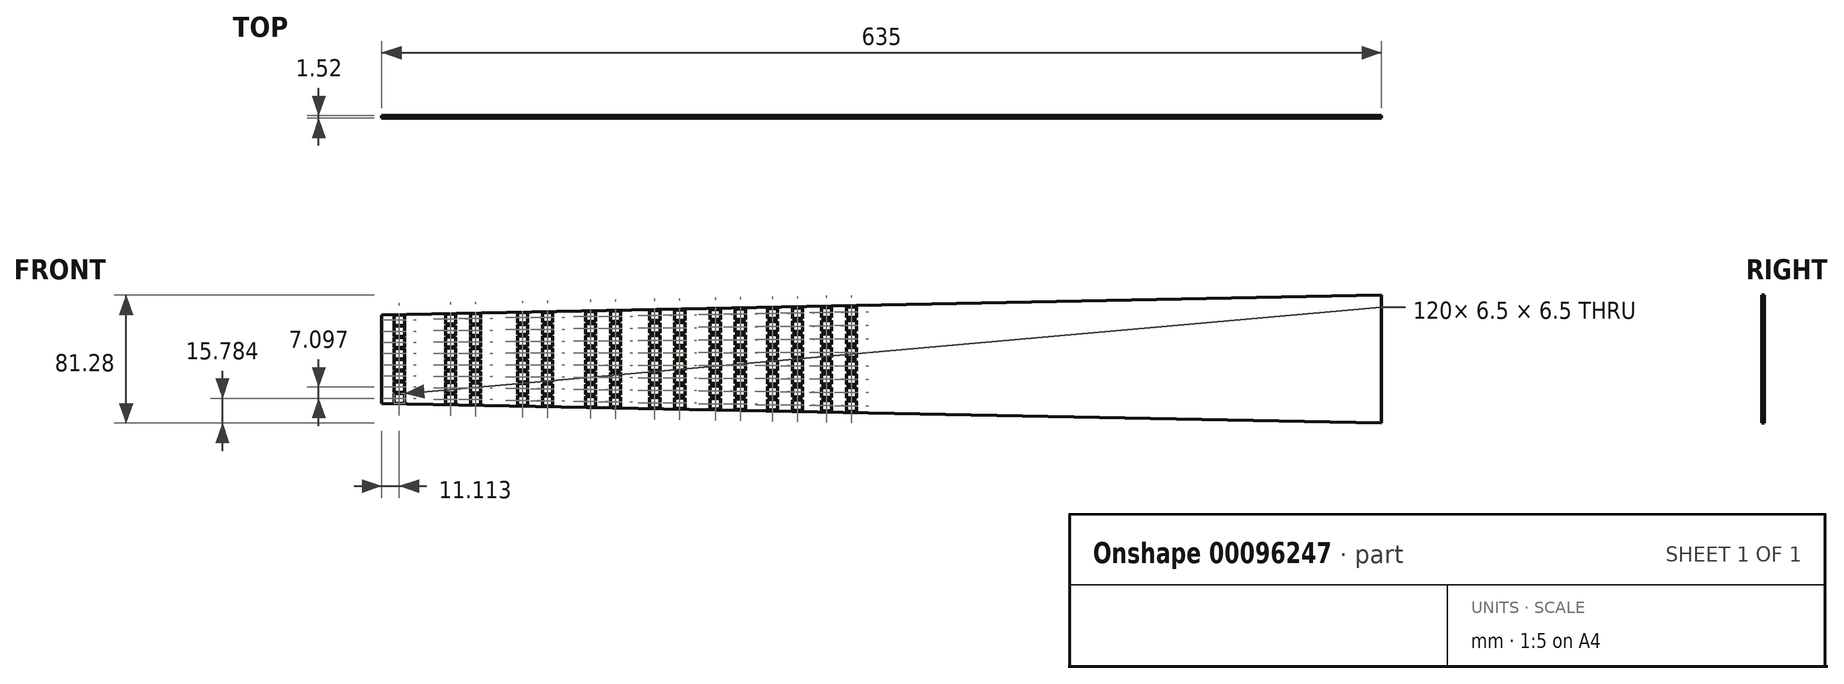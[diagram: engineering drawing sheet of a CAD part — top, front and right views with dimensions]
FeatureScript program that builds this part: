
annotation { "Feature Type Name" : "Feature", "Feature Type Description" : "" }
export const myFeature = defineFeature(function(context is Context, id is Id, definition is map)
    precondition{}
    {
        {
            var Q0;
            Q0=qCreatedBy(makeId("Front.planeOp"),FACE);
            var sketch = newSketch(context, id + "F0", { "sketchPlane" : qUnion([Q0])});
            skLineSegment(sketch, "E0", {"start": v(0, 0) * mm, "end": v(0, 56.39) * mm});
            skLineSegment(sketch, "E1", {"start": v(0, 56.39) * mm, "end": v(304.8, 62.36) * mm});
            skLineSegment(sketch, "E2", {"start": v(635, 68.83) * mm, "end": v(635, -12.45) * mm});
            skLineSegment(sketch, "E3", {"start": v(635, -12.45) * mm, "end": v(304.8, -5.97) * mm});
            skLineSegment(sketch, "E4", {"start": v(0, 28.2) * mm, "end": v(897.35, 28.2) * mm, "construction": true});
            skLineSegment(sketch, "E5", {"start": v(0, 3.52) * mm, "end": v(635, -7.37) * mm, "construction": true});
            skLineSegment(sketch, "E6", {"start": v(0, 10.57) * mm, "end": v(635, 2.8) * mm, "construction": true});
            skLineSegment(sketch, "E7", {"start": v(0, 17.62) * mm, "end": v(635, 12.95) * mm, "construction": true});
            skLineSegment(sketch, "E8", {"start": v(0, 24.67) * mm, "end": v(635, 23.11) * mm, "construction": true});
            skLineSegment(sketch, "E9", {"start": v(11.11, -8.07) * mm, "end": v(11.11, 65.52) * mm, "construction": true});
            skLineSegment(sketch, "E10", {"start": v(59.58, -8.48) * mm, "end": v(59.58, 66.34) * mm, "construction": true});
            skLineSegment(sketch, "E11", {"start": v(43.7, -5.78) * mm, "end": v(43.7, 64.91) * mm, "construction": true});
            skPoint(sketch, "E12", {"position": v(11.11, 3.33) * mm});
            skLineSegment(sketch, "E13.bottom", {"start": v(7.86, 6.58) * mm, "end": v(14.36, 6.58) * mm});
            skLineSegment(sketch, "E13.top", {"start": v(7.86, 0.08) * mm, "end": v(14.36, 0.08) * mm});
            skLineSegment(sketch, "E13.left", {"start": v(7.86, 6.58) * mm, "end": v(7.86, 0.08) * mm});
            skLineSegment(sketch, "E13.right", {"start": v(14.36, 6.58) * mm, "end": v(14.36, 0.08) * mm});
            skLineSegment(sketch, "E14.direction2", {"start": v(7.86, 6.58) * mm, "end": v(7.86, 13.7) * mm, "construction": true});
            skLineSegment(sketch, "E15.bottom", {"start": v(40.46, 6.02) * mm, "end": v(46.96, 6.02) * mm});
            skLineSegment(sketch, "E15.top", {"start": v(40.46, -0.48) * mm, "end": v(46.96, -0.48) * mm});
            skLineSegment(sketch, "E15.left", {"start": v(40.46, 6.02) * mm, "end": v(40.46, -0.48) * mm});
            skLineSegment(sketch, "E15.right", {"start": v(46.96, 6.02) * mm, "end": v(46.96, -0.48) * mm});
            skPoint(sketch, "E15.middle", {"position": v(43.7, 2.77) * mm});
            skLineSegment(sketch, "E16.bottom", {"start": v(62.83, 5.75) * mm, "end": v(56.33, 5.75) * mm});
            skLineSegment(sketch, "E16.top", {"start": v(62.83, -0.75) * mm, "end": v(56.33, -0.75) * mm});
            skLineSegment(sketch, "E16.left", {"start": v(62.83, 5.75) * mm, "end": v(62.83, -0.75) * mm});
            skLineSegment(sketch, "E16.right", {"start": v(56.33, 5.75) * mm, "end": v(56.33, -0.75) * mm});
            skPoint(sketch, "E16.middle", {"position": v(59.58, 2.5) * mm});
            skPoint(sketch, "E17", {"position": v(43.7, 10.04) * mm});
            skPoint(sketch, "E18", {"position": v(59.58, 9.84) * mm});
            skLineSegment(sketch, "E19", {"start": v(89.46, -9.6) * mm, "end": v(89.46, 71.58) * mm, "construction": true});
            skLineSegment(sketch, "E20", {"start": v(105.33, -10.34) * mm, "end": v(105.33, 69.93) * mm, "construction": true});
            skLineSegment(sketch, "E21", {"start": v(132.64, -17.59) * mm, "end": v(132.64, 74.26) * mm, "construction": true});
            skLineSegment(sketch, "E22", {"start": v(148.51, -17.59) * mm, "end": v(148.51, 69.02) * mm, "construction": true});
            skLineSegment(sketch, "E23", {"start": v(173.4, -18.82) * mm, "end": v(173.4, 73.33) * mm, "construction": true});
            skLineSegment(sketch, "E24", {"start": v(189.27, -16.66) * mm, "end": v(189.27, 66.86) * mm, "construction": true});
            skLineSegment(sketch, "E25", {"start": v(451.27, -15.83) * mm, "end": v(451.27, 70.28) * mm, "construction": true});
            skLineSegment(sketch, "E26", {"start": v(227.74, -18.15) * mm, "end": v(227.74, 69.99) * mm, "construction": true});
            skLineSegment(sketch, "E27", {"start": v(264.05, -13.9) * mm, "end": v(264.05, 74.15) * mm, "construction": true});
            skLineSegment(sketch, "E28", {"start": v(298.33, -16.5) * mm, "end": v(298.33, 71.54) * mm, "construction": true});
            skLineSegment(sketch, "E29", {"start": v(330.68, -19.56) * mm, "end": v(330.68, 75.46) * mm, "construction": true});
            skLineSegment(sketch, "E30", {"start": v(361.21, -17.9) * mm, "end": v(361.21, 72.97) * mm, "construction": true});
            skLineSegment(sketch, "E31", {"start": v(390.03, -19.02) * mm, "end": v(390.03, 73.96) * mm, "construction": true});
            skLineSegment(sketch, "E32", {"start": v(417.24, -23.13) * mm, "end": v(417.24, 74.37) * mm, "construction": true});
            skLineSegment(sketch, "E33", {"start": v(442.91, -24.9) * mm, "end": v(442.91, 73.26) * mm, "construction": true});
            skLineSegment(sketch, "E34", {"start": v(467.15, -27.86) * mm, "end": v(467.15, 72.83) * mm, "construction": true});
            skLineSegment(sketch, "E35", {"start": v(492.88, -29.16) * mm, "end": v(492.88, 78.06) * mm, "construction": true});
            skLineSegment(sketch, "E36", {"start": v(513.87, -22.04) * mm, "end": v(513.87, 76.59) * mm, "construction": true});
            skLineSegment(sketch, "E37", {"start": v(533.67, -25.93) * mm, "end": v(533.67, 79.32) * mm, "construction": true});
            skLineSegment(sketch, "E38", {"start": v(602.4, -21.27) * mm, "end": v(602.4, 83.2) * mm, "construction": true});
            skLineSegment(sketch, "E39", {"start": v(570.01, -19.88) * mm, "end": v(570.01, 78.37) * mm, "construction": true});
            skLineSegment(sketch, "E40", {"start": v(586.67, -17.8) * mm, "end": v(586.67, 83.9) * mm, "construction": true});
            skLineSegment(sketch, "E41", {"start": v(552.37, -18.5) * mm, "end": v(552.37, 94.16) * mm, "construction": true});
            skPoint(sketch, "E42", {"position": v(89.46, 2) * mm});
            skPoint(sketch, "E43", {"position": v(89.46, 9.48) * mm});
            skPoint(sketch, "E44", {"position": v(105.33, 9.28) * mm});
            skPoint(sketch, "E45", {"position": v(105.33, 1.72) * mm});
            skPoint(sketch, "E46", {"position": v(132.64, 8.95) * mm});
            skPoint(sketch, "E47", {"position": v(132.64, 1.25) * mm});
            skPoint(sketch, "E48", {"position": v(148.51, 8.75) * mm});
            skPoint(sketch, "E49", {"position": v(148.51, 0.98) * mm});
            skPoint(sketch, "E50", {"position": v(173.4, 8.45) * mm});
            skPoint(sketch, "E51", {"position": v(173.4, 0.55) * mm});
            skPoint(sketch, "E52", {"position": v(189.27, 8.25) * mm});
            skPoint(sketch, "E53", {"position": v(227.74, 7.78) * mm});
            skPoint(sketch, "E54", {"position": v(227.74, -0.38) * mm});
            skLineSegment(sketch, "E55", {"start": v(304.8, -5.97) * mm, "end": v(304.8, 62.36) * mm});
            skLineSegment(sketch, "E56", {"start": v(211.87, -18.15) * mm, "end": v(211.87, 88.54) * mm, "construction": true});
            skLineSegment(sketch, "E57", {"start": v(248.18, -17.72) * mm, "end": v(248.18, 84.91) * mm, "construction": true});
            skLineSegment(sketch, "E58", {"start": v(282.45, -20.3) * mm, "end": v(282.45, 79.21) * mm, "construction": true});
            skPoint(sketch, "E59", {"position": v(298.33, -1.6) * mm});
            skPoint(sketch, "E60", {"position": v(298.33, 6.92) * mm});
            skPoint(sketch, "E61", {"position": v(282.45, 7.11) * mm});
            skPoint(sketch, "E62", {"position": v(282.45, -1.32) * mm});
            skPoint(sketch, "E63", {"position": v(264.05, -1) * mm});
            skPoint(sketch, "E64", {"position": v(264.05, 7.34) * mm});
            skPoint(sketch, "E65", {"position": v(248.18, 7.53) * mm});
            skPoint(sketch, "E66", {"position": v(248.18, -0.73) * mm});
            skPoint(sketch, "E67", {"position": v(211.87, 7.98) * mm});
            skPoint(sketch, "E68", {"position": v(211.87, -0.1) * mm});
            skLineSegment(sketch, "E69.bottom", {"start": v(86.2, 5.24) * mm, "end": v(92.7, 5.24) * mm});
            skLineSegment(sketch, "E69.top", {"start": v(86.2, -1.26) * mm, "end": v(92.7, -1.26) * mm});
            skLineSegment(sketch, "E69.left", {"start": v(86.2, 5.24) * mm, "end": v(86.2, -1.26) * mm});
            skLineSegment(sketch, "E69.right", {"start": v(92.7, 5.24) * mm, "end": v(92.7, -1.26) * mm});
            skLineSegment(sketch, "E70.bottom", {"start": v(102.08, 4.97) * mm, "end": v(108.58, 4.97) * mm});
            skLineSegment(sketch, "E70.top", {"start": v(102.08, -1.53) * mm, "end": v(108.58, -1.53) * mm});
            skLineSegment(sketch, "E70.left", {"start": v(102.08, 4.97) * mm, "end": v(102.08, -1.53) * mm});
            skLineSegment(sketch, "E70.right", {"start": v(108.58, 4.97) * mm, "end": v(108.58, -1.53) * mm});
            skLineSegment(sketch, "E71.bottom", {"start": v(129.39, 4.5) * mm, "end": v(135.89, 4.5) * mm});
            skLineSegment(sketch, "E71.top", {"start": v(129.39, -2) * mm, "end": v(135.89, -2) * mm});
            skLineSegment(sketch, "E71.left", {"start": v(129.39, 4.5) * mm, "end": v(129.39, -2) * mm});
            skLineSegment(sketch, "E71.right", {"start": v(135.89, 4.5) * mm, "end": v(135.89, -2) * mm});
            skLineSegment(sketch, "E72.bottom", {"start": v(145.26, 4.23) * mm, "end": v(151.76, 4.23) * mm});
            skLineSegment(sketch, "E72.top", {"start": v(145.26, -2.27) * mm, "end": v(151.76, -2.27) * mm});
            skLineSegment(sketch, "E72.left", {"start": v(145.26, 4.23) * mm, "end": v(145.26, -2.27) * mm});
            skLineSegment(sketch, "E72.right", {"start": v(151.76, 4.23) * mm, "end": v(151.76, -2.27) * mm});
            skLineSegment(sketch, "E73.bottom", {"start": v(208.62, 3.14) * mm, "end": v(215.12, 3.14) * mm});
            skLineSegment(sketch, "E73.top", {"start": v(208.62, -3.36) * mm, "end": v(215.12, -3.36) * mm});
            skLineSegment(sketch, "E73.left", {"start": v(208.62, 3.14) * mm, "end": v(208.62, -3.36) * mm});
            skLineSegment(sketch, "E73.right", {"start": v(215.12, 3.14) * mm, "end": v(215.12, -3.36) * mm});
            skLineSegment(sketch, "E74.bottom", {"start": v(224.5, 2.87) * mm, "end": v(231, 2.87) * mm});
            skLineSegment(sketch, "E74.top", {"start": v(224.5, -3.63) * mm, "end": v(231, -3.63) * mm});
            skLineSegment(sketch, "E74.left", {"start": v(224.5, 2.87) * mm, "end": v(224.5, -3.63) * mm});
            skLineSegment(sketch, "E74.right", {"start": v(231, 2.87) * mm, "end": v(231, -3.63) * mm});
            skLineSegment(sketch, "E75.bottom", {"start": v(244.93, 2.52) * mm, "end": v(251.43, 2.52) * mm});
            skLineSegment(sketch, "E75.top", {"start": v(244.93, -3.98) * mm, "end": v(251.43, -3.98) * mm});
            skLineSegment(sketch, "E75.left", {"start": v(244.93, 2.52) * mm, "end": v(244.93, -3.98) * mm});
            skLineSegment(sketch, "E75.right", {"start": v(251.43, 2.52) * mm, "end": v(251.43, -3.98) * mm});
            skLineSegment(sketch, "E76.bottom", {"start": v(260.8, 2.25) * mm, "end": v(267.3, 2.25) * mm});
            skLineSegment(sketch, "E76.top", {"start": v(260.8, -4.25) * mm, "end": v(267.3, -4.25) * mm});
            skLineSegment(sketch, "E76.left", {"start": v(260.8, 2.25) * mm, "end": v(260.8, -4.25) * mm});
            skLineSegment(sketch, "E76.right", {"start": v(267.3, 2.25) * mm, "end": v(267.3, -4.25) * mm});
            skLineSegment(sketch, "E77.bottom", {"start": v(279.2, 1.93) * mm, "end": v(285.7, 1.93) * mm});
            skLineSegment(sketch, "E77.top", {"start": v(279.2, -4.57) * mm, "end": v(285.7, -4.57) * mm});
            skLineSegment(sketch, "E77.left", {"start": v(279.2, 1.93) * mm, "end": v(279.2, -4.57) * mm});
            skLineSegment(sketch, "E77.right", {"start": v(285.7, 1.93) * mm, "end": v(285.7, -4.57) * mm});
            skLineSegment(sketch, "E78.bottom", {"start": v(295.08, 1.66) * mm, "end": v(301.58, 1.66) * mm});
            skLineSegment(sketch, "E78.top", {"start": v(295.08, -4.84) * mm, "end": v(301.58, -4.84) * mm});
            skLineSegment(sketch, "E78.left", {"start": v(295.08, 1.66) * mm, "end": v(295.08, -4.84) * mm});
            skLineSegment(sketch, "E78.right", {"start": v(301.58, 1.66) * mm, "end": v(301.58, -4.84) * mm});
            skLineSegment(sketch, "E79.bottom", {"start": v(170.14, 3.8) * mm, "end": v(176.64, 3.8) * mm});
            skLineSegment(sketch, "E79.top", {"start": v(170.14, -2.7) * mm, "end": v(176.64, -2.7) * mm});
            skLineSegment(sketch, "E79.left", {"start": v(170.14, 3.8) * mm, "end": v(170.14, -2.7) * mm});
            skLineSegment(sketch, "E79.right", {"start": v(176.64, 3.8) * mm, "end": v(176.64, -2.7) * mm});
            skPoint(sketch, "E80", {"position": v(304.8, 62.36) * mm});
            skPoint(sketch, "E81", {"position": v(304.8, -5.97) * mm});
            skPoint(sketch, "E82.orphan", {"position": v(304.8, 80.2) * mm});
            skLineSegment(sketch, "E83", {"start": v(304.8, 62.36) * mm, "end": v(635, 68.83) * mm});
            skLineSegment(sketch, "E84", {"start": v(304.8, -5.97) * mm, "end": v(0, 0) * mm});
            skLineSegment(sketch, "E85.0.1.0", {"start": v(40.46, 13.31) * mm, "end": v(46.96, 13.31) * mm});
            skLineSegment(sketch, "E85.0.1.1", {"start": v(40.46, 13.31) * mm, "end": v(40.46, 6.81) * mm});
            skLineSegment(sketch, "E85.0.1.2", {"start": v(46.96, 13.31) * mm, "end": v(46.96, 6.81) * mm});
            skLineSegment(sketch, "E85.0.1.3", {"start": v(40.46, 6.81) * mm, "end": v(46.96, 6.81) * mm});
            skLineSegment(sketch, "E85.0.2.0", {"start": v(40.46, 20.6) * mm, "end": v(46.96, 20.6) * mm});
            skLineSegment(sketch, "E85.0.2.1", {"start": v(40.46, 20.6) * mm, "end": v(40.46, 14.1) * mm});
            skLineSegment(sketch, "E85.0.2.2", {"start": v(46.96, 20.6) * mm, "end": v(46.96, 14.1) * mm});
            skLineSegment(sketch, "E85.0.2.3", {"start": v(40.46, 14.1) * mm, "end": v(46.96, 14.1) * mm});
            skLineSegment(sketch, "E85.0.3.0", {"start": v(40.46, 27.89) * mm, "end": v(46.96, 27.89) * mm});
            skLineSegment(sketch, "E85.0.3.1", {"start": v(40.46, 27.89) * mm, "end": v(40.46, 21.39) * mm});
            skLineSegment(sketch, "E85.0.3.2", {"start": v(46.96, 27.89) * mm, "end": v(46.96, 21.39) * mm});
            skLineSegment(sketch, "E85.0.3.3", {"start": v(40.46, 21.39) * mm, "end": v(46.96, 21.39) * mm});
            skLineSegment(sketch, "E85.direction1", {"start": v(40.46, 6.02) * mm, "end": v(65.86, 6.02) * mm, "construction": true});
            skLineSegment(sketch, "E85.direction2", {"start": v(40.46, 6.02) * mm, "end": v(40.46, 13.31) * mm, "construction": true});
            skLineSegment(sketch, "E86.0.1.0", {"start": v(56.33, 13.1) * mm, "end": v(56.33, 6.6) * mm});
            skLineSegment(sketch, "E86.0.1.1", {"start": v(62.83, 6.6) * mm, "end": v(56.33, 6.6) * mm});
            skLineSegment(sketch, "E86.0.1.2", {"start": v(62.83, 13.1) * mm, "end": v(56.33, 13.1) * mm});
            skLineSegment(sketch, "E86.0.1.3", {"start": v(62.83, 13.1) * mm, "end": v(62.83, 6.6) * mm});
            skPoint(sketch, "E86.0.1.4", {"position": v(59.58, 9.85) * mm});
            skLineSegment(sketch, "E86.0.2.0", {"start": v(56.33, 20.45) * mm, "end": v(56.33, 13.95) * mm});
            skLineSegment(sketch, "E86.0.2.1", {"start": v(62.83, 13.95) * mm, "end": v(56.33, 13.95) * mm});
            skLineSegment(sketch, "E86.0.2.2", {"start": v(62.83, 20.45) * mm, "end": v(56.33, 20.45) * mm});
            skLineSegment(sketch, "E86.0.2.3", {"start": v(62.83, 20.45) * mm, "end": v(62.83, 13.95) * mm});
            skPoint(sketch, "E86.0.2.4", {"position": v(59.58, 17.2) * mm});
            skLineSegment(sketch, "E86.0.3.0", {"start": v(56.33, 27.8) * mm, "end": v(56.33, 21.3) * mm});
            skLineSegment(sketch, "E86.0.3.1", {"start": v(62.83, 21.3) * mm, "end": v(56.33, 21.3) * mm});
            skLineSegment(sketch, "E86.0.3.2", {"start": v(62.83, 27.8) * mm, "end": v(56.33, 27.8) * mm});
            skLineSegment(sketch, "E86.0.3.3", {"start": v(62.83, 27.8) * mm, "end": v(62.83, 21.3) * mm});
            skPoint(sketch, "E86.0.3.4", {"position": v(59.58, 24.55) * mm});
            skLineSegment(sketch, "E86.direction1", {"start": v(56.33, -0.75) * mm, "end": v(83.32, -0.75) * mm, "construction": true});
            skLineSegment(sketch, "E86.direction2", {"start": v(56.33, -0.75) * mm, "end": v(56.33, 6.6) * mm, "construction": true});
            skLineSegment(sketch, "E87.0.1.0", {"start": v(86.2, 6.25) * mm, "end": v(92.7, 6.25) * mm});
            skLineSegment(sketch, "E87.0.1.1", {"start": v(92.7, 12.75) * mm, "end": v(92.7, 6.25) * mm});
            skPoint(sketch, "E87.0.1.2", {"position": v(89.46, 9.5) * mm});
            skLineSegment(sketch, "E87.0.1.3", {"start": v(86.2, 12.75) * mm, "end": v(86.2, 6.25) * mm});
            skLineSegment(sketch, "E87.0.1.4", {"start": v(86.2, 12.75) * mm, "end": v(92.7, 12.75) * mm});
            skPoint(sketch, "E87.0.1.5", {"position": v(89.46, 9.5) * mm});
            skLineSegment(sketch, "E87.0.2.0", {"start": v(86.2, 13.76) * mm, "end": v(92.7, 13.76) * mm});
            skLineSegment(sketch, "E87.0.2.1", {"start": v(92.7, 20.26) * mm, "end": v(92.7, 13.76) * mm});
            skPoint(sketch, "E87.0.2.2", {"position": v(89.46, 17.01) * mm});
            skLineSegment(sketch, "E87.0.2.3", {"start": v(86.2, 20.26) * mm, "end": v(86.2, 13.76) * mm});
            skLineSegment(sketch, "E87.0.2.4", {"start": v(86.2, 20.26) * mm, "end": v(92.7, 20.26) * mm});
            skPoint(sketch, "E87.0.2.5", {"position": v(89.46, 17.01) * mm});
            skLineSegment(sketch, "E87.0.3.0", {"start": v(86.2, 21.27) * mm, "end": v(92.7, 21.27) * mm});
            skLineSegment(sketch, "E87.0.3.1", {"start": v(92.7, 27.77) * mm, "end": v(92.7, 21.27) * mm});
            skPoint(sketch, "E87.0.3.2", {"position": v(89.46, 24.52) * mm});
            skLineSegment(sketch, "E87.0.3.3", {"start": v(86.2, 27.77) * mm, "end": v(86.2, 21.27) * mm});
            skLineSegment(sketch, "E87.0.3.4", {"start": v(86.2, 27.77) * mm, "end": v(92.7, 27.77) * mm});
            skPoint(sketch, "E87.0.3.5", {"position": v(89.46, 24.52) * mm});
            skLineSegment(sketch, "E87.direction1", {"start": v(86.2, -1.26) * mm, "end": v(111.6, -1.26) * mm, "construction": true});
            skLineSegment(sketch, "E87.direction2", {"start": v(86.2, -1.26) * mm, "end": v(86.2, 6.25) * mm, "construction": true});
            skLineSegment(sketch, "E88.0.1.0", {"start": v(102.08, 6.04) * mm, "end": v(108.58, 6.04) * mm});
            skLineSegment(sketch, "E88.0.1.1", {"start": v(102.08, 12.54) * mm, "end": v(102.08, 6.04) * mm});
            skLineSegment(sketch, "E88.0.1.2", {"start": v(102.08, 12.54) * mm, "end": v(108.58, 12.54) * mm});
            skLineSegment(sketch, "E88.0.1.3", {"start": v(108.58, 12.54) * mm, "end": v(108.58, 6.04) * mm});
            skPoint(sketch, "E88.0.1.4", {"position": v(105.33, 9.29) * mm});
            skPoint(sketch, "E88.0.1.5", {"position": v(105.33, 9.29) * mm});
            skLineSegment(sketch, "E88.0.2.0", {"start": v(102.08, 13.61) * mm, "end": v(108.58, 13.61) * mm});
            skLineSegment(sketch, "E88.0.2.1", {"start": v(102.08, 20.11) * mm, "end": v(102.08, 13.61) * mm});
            skLineSegment(sketch, "E88.0.2.2", {"start": v(102.08, 20.11) * mm, "end": v(108.58, 20.11) * mm});
            skLineSegment(sketch, "E88.0.2.3", {"start": v(108.58, 20.11) * mm, "end": v(108.58, 13.61) * mm});
            skPoint(sketch, "E88.0.2.4", {"position": v(105.33, 16.86) * mm});
            skPoint(sketch, "E88.0.2.5", {"position": v(105.33, 16.86) * mm});
            skLineSegment(sketch, "E88.0.3.0", {"start": v(102.08, 21.18) * mm, "end": v(108.58, 21.18) * mm});
            skLineSegment(sketch, "E88.0.3.1", {"start": v(102.08, 27.68) * mm, "end": v(102.08, 21.18) * mm});
            skLineSegment(sketch, "E88.0.3.2", {"start": v(102.08, 27.68) * mm, "end": v(108.58, 27.68) * mm});
            skLineSegment(sketch, "E88.0.3.3", {"start": v(108.58, 27.68) * mm, "end": v(108.58, 21.18) * mm});
            skPoint(sketch, "E88.0.3.4", {"position": v(105.33, 24.43) * mm});
            skPoint(sketch, "E88.0.3.5", {"position": v(105.33, 24.43) * mm});
            skLineSegment(sketch, "E88.direction1", {"start": v(102.08, -1.53) * mm, "end": v(127.48, -1.53) * mm, "construction": true});
            skLineSegment(sketch, "E88.direction2", {"start": v(102.08, -1.53) * mm, "end": v(102.08, 6.04) * mm, "construction": true});
            skLineSegment(sketch, "E89.0.0.4", {"start": v(86.2, 28.78) * mm, "end": v(92.7, 28.78) * mm});
            skLineSegment(sketch, "E89.3.0.4", {"start": v(92.7, 35.28) * mm, "end": v(92.7, 28.78) * mm});
            skPoint(sketch, "E89.6.0.4", {"position": v(89.46, 32.03) * mm});
            skLineSegment(sketch, "E89.7.0.4", {"start": v(86.2, 35.28) * mm, "end": v(86.2, 28.78) * mm});
            skLineSegment(sketch, "E89.10.0.4", {"start": v(86.2, 35.28) * mm, "end": v(92.7, 35.28) * mm});
            skPoint(sketch, "E89.13.0.4", {"position": v(89.46, 32.03) * mm});
            skLineSegment(sketch, "E89.0.0.5", {"start": v(86.2, 36.3) * mm, "end": v(92.7, 36.3) * mm});
            skLineSegment(sketch, "E89.3.0.5", {"start": v(92.7, 42.8) * mm, "end": v(92.7, 36.3) * mm});
            skPoint(sketch, "E89.6.0.5", {"position": v(89.46, 39.54) * mm});
            skLineSegment(sketch, "E89.7.0.5", {"start": v(86.2, 42.8) * mm, "end": v(86.2, 36.3) * mm});
            skLineSegment(sketch, "E89.10.0.5", {"start": v(86.2, 42.8) * mm, "end": v(92.7, 42.8) * mm});
            skPoint(sketch, "E89.13.0.5", {"position": v(89.46, 39.54) * mm});
            skLineSegment(sketch, "E89.0.0.6", {"start": v(86.2, 43.8) * mm, "end": v(92.7, 43.8) * mm});
            skLineSegment(sketch, "E89.3.0.6", {"start": v(92.7, 50.3) * mm, "end": v(92.7, 43.8) * mm});
            skPoint(sketch, "E89.6.0.6", {"position": v(89.46, 47.05) * mm});
            skLineSegment(sketch, "E89.7.0.6", {"start": v(86.2, 50.3) * mm, "end": v(86.2, 43.8) * mm});
            skLineSegment(sketch, "E89.10.0.6", {"start": v(86.2, 50.3) * mm, "end": v(92.7, 50.3) * mm});
            skPoint(sketch, "E89.13.0.6", {"position": v(89.46, 47.05) * mm});
            skLineSegment(sketch, "E89.0.0.7", {"start": v(86.2, 51.32) * mm, "end": v(92.7, 51.32) * mm});
            skLineSegment(sketch, "E89.3.0.7", {"start": v(92.7, 57.82) * mm, "end": v(92.7, 51.32) * mm});
            skPoint(sketch, "E89.6.0.7", {"position": v(89.46, 54.57) * mm});
            skLineSegment(sketch, "E89.7.0.7", {"start": v(86.2, 57.82) * mm, "end": v(86.2, 51.32) * mm});
            skLineSegment(sketch, "E89.10.0.7", {"start": v(86.2, 57.82) * mm, "end": v(92.7, 57.82) * mm});
            skPoint(sketch, "E89.13.0.7", {"position": v(89.46, 54.57) * mm});
            skLineSegment(sketch, "E90.0.0.4", {"start": v(40.46, 35.17) * mm, "end": v(46.96, 35.17) * mm});
            skLineSegment(sketch, "E90.3.0.4", {"start": v(40.46, 35.17) * mm, "end": v(40.46, 28.67) * mm});
            skLineSegment(sketch, "E90.6.0.4", {"start": v(46.96, 35.17) * mm, "end": v(46.96, 28.67) * mm});
            skLineSegment(sketch, "E90.9.0.4", {"start": v(40.46, 28.67) * mm, "end": v(46.96, 28.67) * mm});
            skLineSegment(sketch, "E90.0.0.5", {"start": v(40.46, 42.46) * mm, "end": v(46.96, 42.46) * mm});
            skLineSegment(sketch, "E90.3.0.5", {"start": v(40.46, 42.46) * mm, "end": v(40.46, 35.96) * mm});
            skLineSegment(sketch, "E90.6.0.5", {"start": v(46.96, 42.46) * mm, "end": v(46.96, 35.96) * mm});
            skLineSegment(sketch, "E90.9.0.5", {"start": v(40.46, 35.96) * mm, "end": v(46.96, 35.96) * mm});
            skLineSegment(sketch, "E90.0.0.6", {"start": v(40.46, 49.75) * mm, "end": v(46.96, 49.75) * mm});
            skLineSegment(sketch, "E90.3.0.6", {"start": v(40.46, 49.75) * mm, "end": v(40.46, 43.25) * mm});
            skLineSegment(sketch, "E90.6.0.6", {"start": v(46.96, 49.75) * mm, "end": v(46.96, 43.25) * mm});
            skLineSegment(sketch, "E90.9.0.6", {"start": v(40.46, 43.25) * mm, "end": v(46.96, 43.25) * mm});
            skLineSegment(sketch, "E90.0.0.7", {"start": v(40.46, 57.04) * mm, "end": v(46.96, 57.04) * mm});
            skLineSegment(sketch, "E90.3.0.7", {"start": v(40.46, 57.04) * mm, "end": v(40.46, 50.54) * mm});
            skLineSegment(sketch, "E90.6.0.7", {"start": v(46.96, 57.04) * mm, "end": v(46.96, 50.54) * mm});
            skLineSegment(sketch, "E90.9.0.7", {"start": v(40.46, 50.54) * mm, "end": v(46.96, 50.54) * mm});
            skLineSegment(sketch, "E91.0.0.4", {"start": v(56.33, 35.15) * mm, "end": v(56.33, 28.65) * mm});
            skLineSegment(sketch, "E91.3.0.4", {"start": v(62.83, 28.65) * mm, "end": v(56.33, 28.65) * mm});
            skLineSegment(sketch, "E91.6.0.4", {"start": v(62.83, 35.15) * mm, "end": v(56.33, 35.15) * mm});
            skLineSegment(sketch, "E91.9.0.4", {"start": v(62.83, 35.15) * mm, "end": v(62.83, 28.65) * mm});
            skPoint(sketch, "E91.12.0.4", {"position": v(59.58, 31.9) * mm});
            skLineSegment(sketch, "E91.0.0.5", {"start": v(56.33, 42.5) * mm, "end": v(56.33, 36) * mm});
            skLineSegment(sketch, "E91.3.0.5", {"start": v(62.83, 36) * mm, "end": v(56.33, 36) * mm});
            skLineSegment(sketch, "E91.6.0.5", {"start": v(62.83, 42.5) * mm, "end": v(56.33, 42.5) * mm});
            skLineSegment(sketch, "E91.9.0.5", {"start": v(62.83, 42.5) * mm, "end": v(62.83, 36) * mm});
            skPoint(sketch, "E91.12.0.5", {"position": v(59.58, 39.24) * mm});
            skLineSegment(sketch, "E91.0.0.6", {"start": v(56.33, 49.84) * mm, "end": v(56.33, 43.34) * mm});
            skLineSegment(sketch, "E91.3.0.6", {"start": v(62.83, 43.34) * mm, "end": v(56.33, 43.34) * mm});
            skLineSegment(sketch, "E91.6.0.6", {"start": v(62.83, 49.84) * mm, "end": v(56.33, 49.84) * mm});
            skLineSegment(sketch, "E91.9.0.6", {"start": v(62.83, 49.84) * mm, "end": v(62.83, 43.34) * mm});
            skPoint(sketch, "E91.12.0.6", {"position": v(59.58, 46.6) * mm});
            skLineSegment(sketch, "E91.0.0.7", {"start": v(56.33, 57.19) * mm, "end": v(56.33, 50.69) * mm});
            skLineSegment(sketch, "E91.3.0.7", {"start": v(62.83, 50.69) * mm, "end": v(56.33, 50.69) * mm});
            skLineSegment(sketch, "E91.6.0.7", {"start": v(62.83, 57.19) * mm, "end": v(56.33, 57.19) * mm});
            skLineSegment(sketch, "E91.9.0.7", {"start": v(62.83, 57.19) * mm, "end": v(62.83, 50.69) * mm});
            skPoint(sketch, "E91.12.0.7", {"position": v(59.58, 53.94) * mm});
            skLineSegment(sketch, "E92.0.0.4", {"start": v(102.08, 28.75) * mm, "end": v(108.58, 28.75) * mm});
            skLineSegment(sketch, "E92.3.0.4", {"start": v(102.08, 35.25) * mm, "end": v(102.08, 28.75) * mm});
            skLineSegment(sketch, "E92.6.0.4", {"start": v(102.08, 35.25) * mm, "end": v(108.58, 35.25) * mm});
            skLineSegment(sketch, "E92.9.0.4", {"start": v(108.58, 35.25) * mm, "end": v(108.58, 28.75) * mm});
            skPoint(sketch, "E92.12.0.4", {"position": v(105.33, 32) * mm});
            skPoint(sketch, "E92.13.0.4", {"position": v(105.33, 32) * mm});
            skLineSegment(sketch, "E92.0.0.5", {"start": v(102.08, 36.33) * mm, "end": v(108.58, 36.33) * mm});
            skLineSegment(sketch, "E92.3.0.5", {"start": v(102.08, 42.83) * mm, "end": v(102.08, 36.33) * mm});
            skLineSegment(sketch, "E92.6.0.5", {"start": v(102.08, 42.83) * mm, "end": v(108.58, 42.83) * mm});
            skLineSegment(sketch, "E92.9.0.5", {"start": v(108.58, 42.83) * mm, "end": v(108.58, 36.33) * mm});
            skPoint(sketch, "E92.12.0.5", {"position": v(105.33, 39.58) * mm});
            skPoint(sketch, "E92.13.0.5", {"position": v(105.33, 39.58) * mm});
            skLineSegment(sketch, "E92.0.0.6", {"start": v(102.08, 43.9) * mm, "end": v(108.58, 43.9) * mm});
            skLineSegment(sketch, "E92.3.0.6", {"start": v(102.08, 50.4) * mm, "end": v(102.08, 43.9) * mm});
            skLineSegment(sketch, "E92.6.0.6", {"start": v(102.08, 50.4) * mm, "end": v(108.58, 50.4) * mm});
            skLineSegment(sketch, "E92.9.0.6", {"start": v(108.58, 50.4) * mm, "end": v(108.58, 43.9) * mm});
            skPoint(sketch, "E92.12.0.6", {"position": v(105.33, 47.15) * mm});
            skPoint(sketch, "E92.13.0.6", {"position": v(105.33, 47.15) * mm});
            skLineSegment(sketch, "E92.0.0.7", {"start": v(102.08, 51.47) * mm, "end": v(108.58, 51.47) * mm});
            skLineSegment(sketch, "E92.3.0.7", {"start": v(102.08, 57.97) * mm, "end": v(102.08, 51.47) * mm});
            skLineSegment(sketch, "E92.6.0.7", {"start": v(102.08, 57.97) * mm, "end": v(108.58, 57.97) * mm});
            skLineSegment(sketch, "E92.9.0.7", {"start": v(108.58, 57.97) * mm, "end": v(108.58, 51.47) * mm});
            skPoint(sketch, "E92.12.0.7", {"position": v(105.33, 54.72) * mm});
            skPoint(sketch, "E92.13.0.7", {"position": v(105.33, 54.72) * mm});
            skLineSegment(sketch, "E93.0.1.0", {"start": v(129.39, 5.72) * mm, "end": v(135.89, 5.72) * mm});
            skPoint(sketch, "E93.0.1.1", {"position": v(132.64, 8.97) * mm});
            skLineSegment(sketch, "E93.0.1.2", {"start": v(129.39, 12.22) * mm, "end": v(135.89, 12.22) * mm});
            skLineSegment(sketch, "E93.0.1.3", {"start": v(135.89, 12.22) * mm, "end": v(135.89, 5.72) * mm});
            skLineSegment(sketch, "E93.0.1.4", {"start": v(129.39, 12.22) * mm, "end": v(129.39, 5.72) * mm});
            skPoint(sketch, "E93.0.1.5", {"position": v(132.64, 8.97) * mm});
            skLineSegment(sketch, "E93.0.2.0", {"start": v(129.39, 13.44) * mm, "end": v(135.89, 13.44) * mm});
            skPoint(sketch, "E93.0.2.1", {"position": v(132.64, 16.7) * mm});
            skLineSegment(sketch, "E93.0.2.2", {"start": v(129.39, 19.94) * mm, "end": v(135.89, 19.94) * mm});
            skLineSegment(sketch, "E93.0.2.3", {"start": v(135.89, 19.94) * mm, "end": v(135.89, 13.44) * mm});
            skLineSegment(sketch, "E93.0.2.4", {"start": v(129.39, 19.94) * mm, "end": v(129.39, 13.44) * mm});
            skPoint(sketch, "E93.0.2.5", {"position": v(132.64, 16.7) * mm});
            skLineSegment(sketch, "E93.0.3.0", {"start": v(129.39, 21.16) * mm, "end": v(135.89, 21.16) * mm});
            skPoint(sketch, "E93.0.3.1", {"position": v(132.64, 24.41) * mm});
            skLineSegment(sketch, "E93.0.3.2", {"start": v(129.39, 27.66) * mm, "end": v(135.89, 27.66) * mm});
            skLineSegment(sketch, "E93.0.3.3", {"start": v(135.89, 27.66) * mm, "end": v(135.89, 21.16) * mm});
            skLineSegment(sketch, "E93.0.3.4", {"start": v(129.39, 27.66) * mm, "end": v(129.39, 21.16) * mm});
            skPoint(sketch, "E93.0.3.5", {"position": v(132.64, 24.41) * mm});
            skLineSegment(sketch, "E93.0.4.0", {"start": v(129.39, 28.89) * mm, "end": v(135.89, 28.89) * mm});
            skPoint(sketch, "E93.0.4.1", {"position": v(132.64, 32.14) * mm});
            skLineSegment(sketch, "E93.0.4.2", {"start": v(129.39, 35.39) * mm, "end": v(135.89, 35.39) * mm});
            skLineSegment(sketch, "E93.0.4.3", {"start": v(135.89, 35.39) * mm, "end": v(135.89, 28.89) * mm});
            skLineSegment(sketch, "E93.0.4.4", {"start": v(129.39, 35.39) * mm, "end": v(129.39, 28.89) * mm});
            skPoint(sketch, "E93.0.4.5", {"position": v(132.64, 32.14) * mm});
            skLineSegment(sketch, "E93.0.5.0", {"start": v(129.39, 36.6) * mm, "end": v(135.89, 36.6) * mm});
            skPoint(sketch, "E93.0.5.1", {"position": v(132.64, 39.86) * mm});
            skLineSegment(sketch, "E93.0.5.2", {"start": v(129.39, 43.1) * mm, "end": v(135.89, 43.1) * mm});
            skLineSegment(sketch, "E93.0.5.3", {"start": v(135.89, 43.1) * mm, "end": v(135.89, 36.6) * mm});
            skLineSegment(sketch, "E93.0.5.4", {"start": v(129.39, 43.1) * mm, "end": v(129.39, 36.6) * mm});
            skPoint(sketch, "E93.0.5.5", {"position": v(132.64, 39.86) * mm});
            skLineSegment(sketch, "E93.0.6.0", {"start": v(129.39, 44.33) * mm, "end": v(135.89, 44.33) * mm});
            skPoint(sketch, "E93.0.6.1", {"position": v(132.64, 47.58) * mm});
            skLineSegment(sketch, "E93.0.6.2", {"start": v(129.39, 50.83) * mm, "end": v(135.89, 50.83) * mm});
            skLineSegment(sketch, "E93.0.6.3", {"start": v(135.89, 50.83) * mm, "end": v(135.89, 44.33) * mm});
            skLineSegment(sketch, "E93.0.6.4", {"start": v(129.39, 50.83) * mm, "end": v(129.39, 44.33) * mm});
            skPoint(sketch, "E93.0.6.5", {"position": v(132.64, 47.58) * mm});
            skLineSegment(sketch, "E93.0.7.0", {"start": v(129.39, 52.05) * mm, "end": v(135.89, 52.05) * mm});
            skPoint(sketch, "E93.0.7.1", {"position": v(132.64, 55.3) * mm});
            skLineSegment(sketch, "E93.0.7.2", {"start": v(129.39, 58.55) * mm, "end": v(135.89, 58.55) * mm});
            skLineSegment(sketch, "E93.0.7.3", {"start": v(135.89, 58.55) * mm, "end": v(135.89, 52.05) * mm});
            skLineSegment(sketch, "E93.0.7.4", {"start": v(129.39, 58.55) * mm, "end": v(129.39, 52.05) * mm});
            skPoint(sketch, "E93.0.7.5", {"position": v(132.64, 55.3) * mm});
            skLineSegment(sketch, "E93.direction1", {"start": v(129.39, -2) * mm, "end": v(154.79, -2) * mm, "construction": true});
            skLineSegment(sketch, "E93.direction2", {"start": v(129.39, -2) * mm, "end": v(129.39, 5.72) * mm, "construction": true});
            skLineSegment(sketch, "E94.0.1.0", {"start": v(145.26, 12.01) * mm, "end": v(145.26, 5.51) * mm});
            skLineSegment(sketch, "E94.0.1.1", {"start": v(145.26, 5.51) * mm, "end": v(151.76, 5.51) * mm});
            skLineSegment(sketch, "E94.0.1.2", {"start": v(151.76, 12.01) * mm, "end": v(151.76, 5.51) * mm});
            skPoint(sketch, "E94.0.1.3", {"position": v(148.51, 8.76) * mm});
            skLineSegment(sketch, "E94.0.1.4", {"start": v(145.26, 12.01) * mm, "end": v(151.76, 12.01) * mm});
            skPoint(sketch, "E94.0.1.5", {"position": v(148.51, 8.76) * mm});
            skLineSegment(sketch, "E94.0.2.0", {"start": v(145.26, 19.8) * mm, "end": v(145.26, 13.3) * mm});
            skLineSegment(sketch, "E94.0.2.1", {"start": v(145.26, 13.3) * mm, "end": v(151.76, 13.3) * mm});
            skLineSegment(sketch, "E94.0.2.2", {"start": v(151.76, 19.8) * mm, "end": v(151.76, 13.3) * mm});
            skPoint(sketch, "E94.0.2.3", {"position": v(148.51, 16.55) * mm});
            skLineSegment(sketch, "E94.0.2.4", {"start": v(145.26, 19.8) * mm, "end": v(151.76, 19.8) * mm});
            skPoint(sketch, "E94.0.2.5", {"position": v(148.51, 16.55) * mm});
            skLineSegment(sketch, "E94.0.3.0", {"start": v(145.26, 27.58) * mm, "end": v(145.26, 21.08) * mm});
            skLineSegment(sketch, "E94.0.3.1", {"start": v(145.26, 21.08) * mm, "end": v(151.76, 21.08) * mm});
            skLineSegment(sketch, "E94.0.3.2", {"start": v(151.76, 27.58) * mm, "end": v(151.76, 21.08) * mm});
            skPoint(sketch, "E94.0.3.3", {"position": v(148.51, 24.33) * mm});
            skLineSegment(sketch, "E94.0.3.4", {"start": v(145.26, 27.58) * mm, "end": v(151.76, 27.58) * mm});
            skPoint(sketch, "E94.0.3.5", {"position": v(148.51, 24.33) * mm});
            skLineSegment(sketch, "E94.0.4.0", {"start": v(145.26, 35.37) * mm, "end": v(145.26, 28.87) * mm});
            skLineSegment(sketch, "E94.0.4.1", {"start": v(145.26, 28.87) * mm, "end": v(151.76, 28.87) * mm});
            skLineSegment(sketch, "E94.0.4.2", {"start": v(151.76, 35.37) * mm, "end": v(151.76, 28.87) * mm});
            skPoint(sketch, "E94.0.4.3", {"position": v(148.51, 32.12) * mm});
            skLineSegment(sketch, "E94.0.4.4", {"start": v(145.26, 35.37) * mm, "end": v(151.76, 35.37) * mm});
            skPoint(sketch, "E94.0.4.5", {"position": v(148.51, 32.12) * mm});
            skLineSegment(sketch, "E94.0.5.0", {"start": v(145.26, 43.15) * mm, "end": v(145.26, 36.65) * mm});
            skLineSegment(sketch, "E94.0.5.1", {"start": v(145.26, 36.65) * mm, "end": v(151.76, 36.65) * mm});
            skLineSegment(sketch, "E94.0.5.2", {"start": v(151.76, 43.15) * mm, "end": v(151.76, 36.65) * mm});
            skPoint(sketch, "E94.0.5.3", {"position": v(148.51, 39.9) * mm});
            skLineSegment(sketch, "E94.0.5.4", {"start": v(145.26, 43.15) * mm, "end": v(151.76, 43.15) * mm});
            skPoint(sketch, "E94.0.5.5", {"position": v(148.51, 39.9) * mm});
            skLineSegment(sketch, "E94.0.6.0", {"start": v(145.26, 50.94) * mm, "end": v(145.26, 44.44) * mm});
            skLineSegment(sketch, "E94.0.6.1", {"start": v(145.26, 44.44) * mm, "end": v(151.76, 44.44) * mm});
            skLineSegment(sketch, "E94.0.6.2", {"start": v(151.76, 50.94) * mm, "end": v(151.76, 44.44) * mm});
            skPoint(sketch, "E94.0.6.3", {"position": v(148.51, 47.69) * mm});
            skLineSegment(sketch, "E94.0.6.4", {"start": v(145.26, 50.94) * mm, "end": v(151.76, 50.94) * mm});
            skPoint(sketch, "E94.0.6.5", {"position": v(148.51, 47.69) * mm});
            skLineSegment(sketch, "E94.0.7.0", {"start": v(145.26, 58.72) * mm, "end": v(145.26, 52.22) * mm});
            skLineSegment(sketch, "E94.0.7.1", {"start": v(145.26, 52.22) * mm, "end": v(151.76, 52.22) * mm});
            skLineSegment(sketch, "E94.0.7.2", {"start": v(151.76, 58.72) * mm, "end": v(151.76, 52.22) * mm});
            skPoint(sketch, "E94.0.7.3", {"position": v(148.51, 55.47) * mm});
            skLineSegment(sketch, "E94.0.7.4", {"start": v(145.26, 58.72) * mm, "end": v(151.76, 58.72) * mm});
            skPoint(sketch, "E94.0.7.5", {"position": v(148.51, 55.47) * mm});
            skLineSegment(sketch, "E94.direction1", {"start": v(145.26, -2.27) * mm, "end": v(172.25, -2.27) * mm, "construction": true});
            skLineSegment(sketch, "E94.direction2", {"start": v(145.26, -2.27) * mm, "end": v(145.26, 5.51) * mm, "construction": true});
            skPoint(sketch, "E95.0.1.0", {"position": v(173.4, 8.47) * mm});
            skLineSegment(sketch, "E95.0.1.1", {"start": v(170.14, 5.22) * mm, "end": v(176.64, 5.22) * mm});
            skLineSegment(sketch, "E95.0.1.2", {"start": v(176.64, 11.72) * mm, "end": v(176.64, 5.22) * mm});
            skLineSegment(sketch, "E95.0.1.3", {"start": v(170.14, 11.72) * mm, "end": v(170.14, 5.22) * mm});
            skLineSegment(sketch, "E95.0.1.4", {"start": v(170.14, 11.72) * mm, "end": v(176.64, 11.72) * mm});
            skPoint(sketch, "E95.0.1.5", {"position": v(173.4, 8.47) * mm});
            skPoint(sketch, "E95.0.1.6", {"position": v(173.4, 8.47) * mm});
            skPoint(sketch, "E95.0.2.0", {"position": v(173.4, 16.4) * mm});
            skLineSegment(sketch, "E95.0.2.1", {"start": v(170.14, 13.15) * mm, "end": v(176.64, 13.15) * mm});
            skLineSegment(sketch, "E95.0.2.2", {"start": v(176.64, 19.65) * mm, "end": v(176.64, 13.15) * mm});
            skLineSegment(sketch, "E95.0.2.3", {"start": v(170.14, 19.65) * mm, "end": v(170.14, 13.15) * mm});
            skLineSegment(sketch, "E95.0.2.4", {"start": v(170.14, 19.65) * mm, "end": v(176.64, 19.65) * mm});
            skPoint(sketch, "E95.0.2.5", {"position": v(173.4, 16.4) * mm});
            skPoint(sketch, "E95.0.2.6", {"position": v(173.4, 16.4) * mm});
            skPoint(sketch, "E95.0.3.0", {"position": v(173.4, 24.32) * mm});
            skLineSegment(sketch, "E95.0.3.1", {"start": v(170.14, 21.07) * mm, "end": v(176.64, 21.07) * mm});
            skLineSegment(sketch, "E95.0.3.2", {"start": v(176.64, 27.57) * mm, "end": v(176.64, 21.07) * mm});
            skLineSegment(sketch, "E95.0.3.3", {"start": v(170.14, 27.57) * mm, "end": v(170.14, 21.07) * mm});
            skLineSegment(sketch, "E95.0.3.4", {"start": v(170.14, 27.57) * mm, "end": v(176.64, 27.57) * mm});
            skPoint(sketch, "E95.0.3.5", {"position": v(173.4, 24.32) * mm});
            skPoint(sketch, "E95.0.3.6", {"position": v(173.4, 24.32) * mm});
            skPoint(sketch, "E95.0.4.0", {"position": v(173.4, 32.24) * mm});
            skLineSegment(sketch, "E95.0.4.1", {"start": v(170.14, 28.99) * mm, "end": v(176.64, 28.99) * mm});
            skLineSegment(sketch, "E95.0.4.2", {"start": v(176.64, 35.49) * mm, "end": v(176.64, 28.99) * mm});
            skLineSegment(sketch, "E95.0.4.3", {"start": v(170.14, 35.49) * mm, "end": v(170.14, 28.99) * mm});
            skLineSegment(sketch, "E95.0.4.4", {"start": v(170.14, 35.49) * mm, "end": v(176.64, 35.49) * mm});
            skPoint(sketch, "E95.0.4.5", {"position": v(173.4, 32.24) * mm});
            skPoint(sketch, "E95.0.4.6", {"position": v(173.4, 32.24) * mm});
            skPoint(sketch, "E95.0.5.0", {"position": v(173.4, 40.16) * mm});
            skLineSegment(sketch, "E95.0.5.1", {"start": v(170.14, 36.91) * mm, "end": v(176.64, 36.91) * mm});
            skLineSegment(sketch, "E95.0.5.2", {"start": v(176.64, 43.41) * mm, "end": v(176.64, 36.91) * mm});
            skLineSegment(sketch, "E95.0.5.3", {"start": v(170.14, 43.41) * mm, "end": v(170.14, 36.91) * mm});
            skLineSegment(sketch, "E95.0.5.4", {"start": v(170.14, 43.41) * mm, "end": v(176.64, 43.41) * mm});
            skPoint(sketch, "E95.0.5.5", {"position": v(173.4, 40.16) * mm});
            skPoint(sketch, "E95.0.5.6", {"position": v(173.4, 40.16) * mm});
            skPoint(sketch, "E95.0.6.0", {"position": v(173.4, 48.08) * mm});
            skLineSegment(sketch, "E95.0.6.1", {"start": v(170.14, 44.83) * mm, "end": v(176.64, 44.83) * mm});
            skLineSegment(sketch, "E95.0.6.2", {"start": v(176.64, 51.33) * mm, "end": v(176.64, 44.83) * mm});
            skLineSegment(sketch, "E95.0.6.3", {"start": v(170.14, 51.33) * mm, "end": v(170.14, 44.83) * mm});
            skLineSegment(sketch, "E95.0.6.4", {"start": v(170.14, 51.33) * mm, "end": v(176.64, 51.33) * mm});
            skPoint(sketch, "E95.0.6.5", {"position": v(173.4, 48.08) * mm});
            skPoint(sketch, "E95.0.6.6", {"position": v(173.4, 48.08) * mm});
            skPoint(sketch, "E95.0.7.0", {"position": v(173.4, 56) * mm});
            skLineSegment(sketch, "E95.0.7.1", {"start": v(170.14, 52.76) * mm, "end": v(176.64, 52.76) * mm});
            skLineSegment(sketch, "E95.0.7.2", {"start": v(176.64, 59.26) * mm, "end": v(176.64, 52.76) * mm});
            skLineSegment(sketch, "E95.0.7.3", {"start": v(170.14, 59.26) * mm, "end": v(170.14, 52.76) * mm});
            skLineSegment(sketch, "E95.0.7.4", {"start": v(170.14, 59.26) * mm, "end": v(176.64, 59.26) * mm});
            skPoint(sketch, "E95.0.7.5", {"position": v(173.4, 56) * mm});
            skPoint(sketch, "E95.0.7.6", {"position": v(173.4, 56) * mm});
            skLineSegment(sketch, "E95.direction1", {"start": v(173.4, 0.55) * mm, "end": v(198.8, 0.55) * mm, "construction": true});
            skLineSegment(sketch, "E95.direction2", {"start": v(173.4, 0.55) * mm, "end": v(173.4, 8.47) * mm, "construction": true});
            skPoint(sketch, "E96", {"position": v(189.27, 0.28) * mm});
            skLineSegment(sketch, "E97.bottom", {"start": v(186.02, 3.53) * mm, "end": v(192.52, 3.53) * mm});
            skLineSegment(sketch, "E97.top", {"start": v(186.02, -2.97) * mm, "end": v(192.52, -2.97) * mm});
            skLineSegment(sketch, "E97.left", {"start": v(186.02, 3.53) * mm, "end": v(186.02, -2.97) * mm});
            skLineSegment(sketch, "E97.right", {"start": v(192.52, 3.53) * mm, "end": v(192.52, -2.97) * mm});
            skLineSegment(sketch, "E98.0.1.0", {"start": v(186.02, 11.51) * mm, "end": v(192.52, 11.51) * mm});
            skLineSegment(sketch, "E98.0.1.1", {"start": v(186.02, 11.51) * mm, "end": v(186.02, 5.01) * mm});
            skLineSegment(sketch, "E98.0.1.2", {"start": v(186.02, 5.01) * mm, "end": v(192.52, 5.01) * mm});
            skPoint(sketch, "E98.0.1.3", {"position": v(189.27, 8.26) * mm});
            skLineSegment(sketch, "E98.0.1.4", {"start": v(192.52, 11.51) * mm, "end": v(192.52, 5.01) * mm});
            skPoint(sketch, "E98.0.1.5", {"position": v(189.27, 8.26) * mm});
            skLineSegment(sketch, "E98.0.2.0", {"start": v(186.02, 19.5) * mm, "end": v(192.52, 19.5) * mm});
            skLineSegment(sketch, "E98.0.2.1", {"start": v(186.02, 19.5) * mm, "end": v(186.02, 13) * mm});
            skLineSegment(sketch, "E98.0.2.2", {"start": v(186.02, 13) * mm, "end": v(192.52, 13) * mm});
            skPoint(sketch, "E98.0.2.3", {"position": v(189.27, 16.24) * mm});
            skLineSegment(sketch, "E98.0.2.4", {"start": v(192.52, 19.5) * mm, "end": v(192.52, 13) * mm});
            skPoint(sketch, "E98.0.2.5", {"position": v(189.27, 16.24) * mm});
            skLineSegment(sketch, "E98.0.3.0", {"start": v(186.02, 27.48) * mm, "end": v(192.52, 27.48) * mm});
            skLineSegment(sketch, "E98.0.3.1", {"start": v(186.02, 27.48) * mm, "end": v(186.02, 20.98) * mm});
            skLineSegment(sketch, "E98.0.3.2", {"start": v(186.02, 20.98) * mm, "end": v(192.52, 20.98) * mm});
            skPoint(sketch, "E98.0.3.3", {"position": v(189.27, 24.23) * mm});
            skLineSegment(sketch, "E98.0.3.4", {"start": v(192.52, 27.48) * mm, "end": v(192.52, 20.98) * mm});
            skPoint(sketch, "E98.0.3.5", {"position": v(189.27, 24.23) * mm});
            skLineSegment(sketch, "E98.0.4.0", {"start": v(186.02, 35.46) * mm, "end": v(192.52, 35.46) * mm});
            skLineSegment(sketch, "E98.0.4.1", {"start": v(186.02, 35.46) * mm, "end": v(186.02, 28.96) * mm});
            skLineSegment(sketch, "E98.0.4.2", {"start": v(186.02, 28.96) * mm, "end": v(192.52, 28.96) * mm});
            skPoint(sketch, "E98.0.4.3", {"position": v(189.27, 32.21) * mm});
            skLineSegment(sketch, "E98.0.4.4", {"start": v(192.52, 35.46) * mm, "end": v(192.52, 28.96) * mm});
            skPoint(sketch, "E98.0.4.5", {"position": v(189.27, 32.21) * mm});
            skLineSegment(sketch, "E98.0.5.0", {"start": v(186.02, 43.44) * mm, "end": v(192.52, 43.44) * mm});
            skLineSegment(sketch, "E98.0.5.1", {"start": v(186.02, 43.44) * mm, "end": v(186.02, 36.94) * mm});
            skLineSegment(sketch, "E98.0.5.2", {"start": v(186.02, 36.94) * mm, "end": v(192.52, 36.94) * mm});
            skPoint(sketch, "E98.0.5.3", {"position": v(189.27, 40.2) * mm});
            skLineSegment(sketch, "E98.0.5.4", {"start": v(192.52, 43.44) * mm, "end": v(192.52, 36.94) * mm});
            skPoint(sketch, "E98.0.5.5", {"position": v(189.27, 40.2) * mm});
            skLineSegment(sketch, "E98.0.6.0", {"start": v(186.02, 51.43) * mm, "end": v(192.52, 51.43) * mm});
            skLineSegment(sketch, "E98.0.6.1", {"start": v(186.02, 51.43) * mm, "end": v(186.02, 44.93) * mm});
            skLineSegment(sketch, "E98.0.6.2", {"start": v(186.02, 44.93) * mm, "end": v(192.52, 44.93) * mm});
            skPoint(sketch, "E98.0.6.3", {"position": v(189.27, 48.18) * mm});
            skLineSegment(sketch, "E98.0.6.4", {"start": v(192.52, 51.43) * mm, "end": v(192.52, 44.93) * mm});
            skPoint(sketch, "E98.0.6.5", {"position": v(189.27, 48.18) * mm});
            skLineSegment(sketch, "E98.0.7.0", {"start": v(186.02, 59.41) * mm, "end": v(192.52, 59.41) * mm});
            skLineSegment(sketch, "E98.0.7.1", {"start": v(186.02, 59.41) * mm, "end": v(186.02, 52.91) * mm});
            skLineSegment(sketch, "E98.0.7.2", {"start": v(186.02, 52.91) * mm, "end": v(192.52, 52.91) * mm});
            skPoint(sketch, "E98.0.7.3", {"position": v(189.27, 56.16) * mm});
            skLineSegment(sketch, "E98.0.7.4", {"start": v(192.52, 59.41) * mm, "end": v(192.52, 52.91) * mm});
            skPoint(sketch, "E98.0.7.5", {"position": v(189.27, 56.16) * mm});
            skLineSegment(sketch, "E98.direction1", {"start": v(186.02, 3.53) * mm, "end": v(211.42, 3.53) * mm, "construction": true});
            skLineSegment(sketch, "E98.direction2", {"start": v(186.02, 3.53) * mm, "end": v(186.02, 11.51) * mm, "construction": true});
            skLineSegment(sketch, "E99.0.1.0", {"start": v(208.62, 11.25) * mm, "end": v(208.62, 4.75) * mm});
            skLineSegment(sketch, "E99.0.1.1", {"start": v(208.62, 4.75) * mm, "end": v(215.12, 4.75) * mm});
            skLineSegment(sketch, "E99.0.1.2", {"start": v(208.62, 11.25) * mm, "end": v(215.12, 11.25) * mm});
            skPoint(sketch, "E99.0.1.3", {"position": v(211.87, 8) * mm});
            skLineSegment(sketch, "E99.0.1.4", {"start": v(215.12, 11.25) * mm, "end": v(215.12, 4.75) * mm});
            skPoint(sketch, "E99.0.1.5", {"position": v(211.87, 8) * mm});
            skLineSegment(sketch, "E99.0.2.0", {"start": v(208.62, 19.36) * mm, "end": v(208.62, 12.86) * mm});
            skLineSegment(sketch, "E99.0.2.1", {"start": v(208.62, 12.86) * mm, "end": v(215.12, 12.86) * mm});
            skLineSegment(sketch, "E99.0.2.2", {"start": v(208.62, 19.36) * mm, "end": v(215.12, 19.36) * mm});
            skPoint(sketch, "E99.0.2.3", {"position": v(211.87, 16.11) * mm});
            skLineSegment(sketch, "E99.0.2.4", {"start": v(215.12, 19.36) * mm, "end": v(215.12, 12.86) * mm});
            skPoint(sketch, "E99.0.2.5", {"position": v(211.87, 16.11) * mm});
            skLineSegment(sketch, "E99.0.3.0", {"start": v(208.62, 27.47) * mm, "end": v(208.62, 20.97) * mm});
            skLineSegment(sketch, "E99.0.3.1", {"start": v(208.62, 20.97) * mm, "end": v(215.12, 20.97) * mm});
            skLineSegment(sketch, "E99.0.3.2", {"start": v(208.62, 27.47) * mm, "end": v(215.12, 27.47) * mm});
            skPoint(sketch, "E99.0.3.3", {"position": v(211.87, 24.22) * mm});
            skLineSegment(sketch, "E99.0.3.4", {"start": v(215.12, 27.47) * mm, "end": v(215.12, 20.97) * mm});
            skPoint(sketch, "E99.0.3.5", {"position": v(211.87, 24.22) * mm});
            skLineSegment(sketch, "E99.0.4.0", {"start": v(208.62, 35.58) * mm, "end": v(208.62, 29.08) * mm});
            skLineSegment(sketch, "E99.0.4.1", {"start": v(208.62, 29.08) * mm, "end": v(215.12, 29.08) * mm});
            skLineSegment(sketch, "E99.0.4.2", {"start": v(208.62, 35.58) * mm, "end": v(215.12, 35.58) * mm});
            skPoint(sketch, "E99.0.4.3", {"position": v(211.87, 32.33) * mm});
            skLineSegment(sketch, "E99.0.4.4", {"start": v(215.12, 35.58) * mm, "end": v(215.12, 29.08) * mm});
            skPoint(sketch, "E99.0.4.5", {"position": v(211.87, 32.33) * mm});
            skLineSegment(sketch, "E99.0.5.0", {"start": v(208.62, 43.7) * mm, "end": v(208.62, 37.2) * mm});
            skLineSegment(sketch, "E99.0.5.1", {"start": v(208.62, 37.2) * mm, "end": v(215.12, 37.2) * mm});
            skLineSegment(sketch, "E99.0.5.2", {"start": v(208.62, 43.7) * mm, "end": v(215.12, 43.7) * mm});
            skPoint(sketch, "E99.0.5.3", {"position": v(211.87, 40.44) * mm});
            skLineSegment(sketch, "E99.0.5.4", {"start": v(215.12, 43.7) * mm, "end": v(215.12, 37.2) * mm});
            skPoint(sketch, "E99.0.5.5", {"position": v(211.87, 40.44) * mm});
            skLineSegment(sketch, "E99.0.6.0", {"start": v(208.62, 51.8) * mm, "end": v(208.62, 45.3) * mm});
            skLineSegment(sketch, "E99.0.6.1", {"start": v(208.62, 45.3) * mm, "end": v(215.12, 45.3) * mm});
            skLineSegment(sketch, "E99.0.6.2", {"start": v(208.62, 51.8) * mm, "end": v(215.12, 51.8) * mm});
            skPoint(sketch, "E99.0.6.3", {"position": v(211.87, 48.55) * mm});
            skLineSegment(sketch, "E99.0.6.4", {"start": v(215.12, 51.8) * mm, "end": v(215.12, 45.3) * mm});
            skPoint(sketch, "E99.0.6.5", {"position": v(211.87, 48.55) * mm});
            skLineSegment(sketch, "E99.0.7.0", {"start": v(208.62, 59.91) * mm, "end": v(208.62, 53.41) * mm});
            skLineSegment(sketch, "E99.0.7.1", {"start": v(208.62, 53.41) * mm, "end": v(215.12, 53.41) * mm});
            skLineSegment(sketch, "E99.0.7.2", {"start": v(208.62, 59.91) * mm, "end": v(215.12, 59.91) * mm});
            skPoint(sketch, "E99.0.7.3", {"position": v(211.87, 56.66) * mm});
            skLineSegment(sketch, "E99.0.7.4", {"start": v(215.12, 59.91) * mm, "end": v(215.12, 53.41) * mm});
            skPoint(sketch, "E99.0.7.5", {"position": v(211.87, 56.66) * mm});
            skLineSegment(sketch, "E99.direction1", {"start": v(208.62, -3.36) * mm, "end": v(234.02, -3.36) * mm, "construction": true});
            skLineSegment(sketch, "E99.direction2", {"start": v(208.62, -3.36) * mm, "end": v(208.62, 4.75) * mm, "construction": true});
            skPoint(sketch, "E100.0.1.0", {"position": v(227.74, 7.79) * mm});
            skLineSegment(sketch, "E100.0.1.1", {"start": v(231, 11.04) * mm, "end": v(231, 4.54) * mm});
            skLineSegment(sketch, "E100.0.1.2", {"start": v(224.5, 11.04) * mm, "end": v(224.5, 4.54) * mm});
            skLineSegment(sketch, "E100.0.1.3", {"start": v(224.5, 11.04) * mm, "end": v(231, 11.04) * mm});
            skLineSegment(sketch, "E100.0.1.4", {"start": v(224.5, 4.54) * mm, "end": v(231, 4.54) * mm});
            skPoint(sketch, "E100.0.1.5", {"position": v(227.74, 7.79) * mm});
            skPoint(sketch, "E100.0.2.0", {"position": v(227.74, 15.96) * mm});
            skLineSegment(sketch, "E100.0.2.1", {"start": v(231, 19.21) * mm, "end": v(231, 12.71) * mm});
            skLineSegment(sketch, "E100.0.2.2", {"start": v(224.5, 19.21) * mm, "end": v(224.5, 12.71) * mm});
            skLineSegment(sketch, "E100.0.2.3", {"start": v(224.5, 19.21) * mm, "end": v(231, 19.21) * mm});
            skLineSegment(sketch, "E100.0.2.4", {"start": v(224.5, 12.71) * mm, "end": v(231, 12.71) * mm});
            skPoint(sketch, "E100.0.2.5", {"position": v(227.74, 15.96) * mm});
            skPoint(sketch, "E100.0.3.0", {"position": v(227.74, 24.13) * mm});
            skLineSegment(sketch, "E100.0.3.1", {"start": v(231, 27.38) * mm, "end": v(231, 20.88) * mm});
            skLineSegment(sketch, "E100.0.3.2", {"start": v(224.5, 27.38) * mm, "end": v(224.5, 20.88) * mm});
            skLineSegment(sketch, "E100.0.3.3", {"start": v(224.5, 27.38) * mm, "end": v(231, 27.38) * mm});
            skLineSegment(sketch, "E100.0.3.4", {"start": v(224.5, 20.88) * mm, "end": v(231, 20.88) * mm});
            skPoint(sketch, "E100.0.3.5", {"position": v(227.74, 24.13) * mm});
            skPoint(sketch, "E100.0.4.0", {"position": v(227.74, 32.3) * mm});
            skLineSegment(sketch, "E100.0.4.1", {"start": v(231, 35.55) * mm, "end": v(231, 29.05) * mm});
            skLineSegment(sketch, "E100.0.4.2", {"start": v(224.5, 35.55) * mm, "end": v(224.5, 29.05) * mm});
            skLineSegment(sketch, "E100.0.4.3", {"start": v(224.5, 35.55) * mm, "end": v(231, 35.55) * mm});
            skLineSegment(sketch, "E100.0.4.4", {"start": v(224.5, 29.05) * mm, "end": v(231, 29.05) * mm});
            skPoint(sketch, "E100.0.4.5", {"position": v(227.74, 32.3) * mm});
            skPoint(sketch, "E100.0.5.0", {"position": v(227.74, 40.47) * mm});
            skLineSegment(sketch, "E100.0.5.1", {"start": v(231, 43.72) * mm, "end": v(231, 37.22) * mm});
            skLineSegment(sketch, "E100.0.5.2", {"start": v(224.5, 43.72) * mm, "end": v(224.5, 37.22) * mm});
            skLineSegment(sketch, "E100.0.5.3", {"start": v(224.5, 43.72) * mm, "end": v(231, 43.72) * mm});
            skLineSegment(sketch, "E100.0.5.4", {"start": v(224.5, 37.22) * mm, "end": v(231, 37.22) * mm});
            skPoint(sketch, "E100.0.5.5", {"position": v(227.74, 40.47) * mm});
            skPoint(sketch, "E100.0.6.0", {"position": v(227.74, 48.65) * mm});
            skLineSegment(sketch, "E100.0.6.1", {"start": v(231, 51.9) * mm, "end": v(231, 45.4) * mm});
            skLineSegment(sketch, "E100.0.6.2", {"start": v(224.5, 51.9) * mm, "end": v(224.5, 45.4) * mm});
            skLineSegment(sketch, "E100.0.6.3", {"start": v(224.5, 51.9) * mm, "end": v(231, 51.9) * mm});
            skLineSegment(sketch, "E100.0.6.4", {"start": v(224.5, 45.4) * mm, "end": v(231, 45.4) * mm});
            skPoint(sketch, "E100.0.6.5", {"position": v(227.74, 48.65) * mm});
            skPoint(sketch, "E100.0.7.0", {"position": v(227.74, 56.82) * mm});
            skLineSegment(sketch, "E100.0.7.1", {"start": v(231, 60.07) * mm, "end": v(231, 53.57) * mm});
            skLineSegment(sketch, "E100.0.7.2", {"start": v(224.5, 60.07) * mm, "end": v(224.5, 53.57) * mm});
            skLineSegment(sketch, "E100.0.7.3", {"start": v(224.5, 60.07) * mm, "end": v(231, 60.07) * mm});
            skLineSegment(sketch, "E100.0.7.4", {"start": v(224.5, 53.57) * mm, "end": v(231, 53.57) * mm});
            skPoint(sketch, "E100.0.7.5", {"position": v(227.74, 56.82) * mm});
            skLineSegment(sketch, "E100.direction1", {"start": v(227.74, -0.38) * mm, "end": v(253.14, -0.38) * mm, "construction": true});
            skLineSegment(sketch, "E100.direction2", {"start": v(227.74, -0.38) * mm, "end": v(227.74, 7.79) * mm, "construction": true});
            skLineSegment(sketch, "E101.0.1.0", {"start": v(251.43, 10.8) * mm, "end": v(251.43, 4.3) * mm});
            skPoint(sketch, "E101.0.1.1", {"position": v(248.18, 7.56) * mm});
            skLineSegment(sketch, "E101.0.1.2", {"start": v(244.93, 10.8) * mm, "end": v(244.93, 4.3) * mm});
            skLineSegment(sketch, "E101.0.1.3", {"start": v(244.93, 4.3) * mm, "end": v(251.43, 4.3) * mm});
            skLineSegment(sketch, "E101.0.1.4", {"start": v(244.93, 10.8) * mm, "end": v(251.43, 10.8) * mm});
            skPoint(sketch, "E101.0.1.5", {"position": v(248.18, 7.56) * mm});
            skLineSegment(sketch, "E101.0.2.0", {"start": v(251.43, 19.1) * mm, "end": v(251.43, 12.6) * mm});
            skPoint(sketch, "E101.0.2.1", {"position": v(248.18, 15.84) * mm});
            skLineSegment(sketch, "E101.0.2.2", {"start": v(244.93, 19.1) * mm, "end": v(244.93, 12.6) * mm});
            skLineSegment(sketch, "E101.0.2.3", {"start": v(244.93, 12.6) * mm, "end": v(251.43, 12.6) * mm});
            skLineSegment(sketch, "E101.0.2.4", {"start": v(244.93, 19.1) * mm, "end": v(251.43, 19.1) * mm});
            skPoint(sketch, "E101.0.2.5", {"position": v(248.18, 15.84) * mm});
            skLineSegment(sketch, "E101.0.3.0", {"start": v(251.43, 27.38) * mm, "end": v(251.43, 20.88) * mm});
            skPoint(sketch, "E101.0.3.1", {"position": v(248.18, 24.13) * mm});
            skLineSegment(sketch, "E101.0.3.2", {"start": v(244.93, 27.38) * mm, "end": v(244.93, 20.88) * mm});
            skLineSegment(sketch, "E101.0.3.3", {"start": v(244.93, 20.88) * mm, "end": v(251.43, 20.88) * mm});
            skLineSegment(sketch, "E101.0.3.4", {"start": v(244.93, 27.38) * mm, "end": v(251.43, 27.38) * mm});
            skPoint(sketch, "E101.0.3.5", {"position": v(248.18, 24.13) * mm});
            skLineSegment(sketch, "E101.0.4.0", {"start": v(251.43, 35.67) * mm, "end": v(251.43, 29.17) * mm});
            skPoint(sketch, "E101.0.4.1", {"position": v(248.18, 32.42) * mm});
            skLineSegment(sketch, "E101.0.4.2", {"start": v(244.93, 35.67) * mm, "end": v(244.93, 29.17) * mm});
            skLineSegment(sketch, "E101.0.4.3", {"start": v(244.93, 29.17) * mm, "end": v(251.43, 29.17) * mm});
            skLineSegment(sketch, "E101.0.4.4", {"start": v(244.93, 35.67) * mm, "end": v(251.43, 35.67) * mm});
            skPoint(sketch, "E101.0.4.5", {"position": v(248.18, 32.42) * mm});
            skLineSegment(sketch, "E101.0.5.0", {"start": v(251.43, 43.96) * mm, "end": v(251.43, 37.46) * mm});
            skPoint(sketch, "E101.0.5.1", {"position": v(248.18, 40.7) * mm});
            skLineSegment(sketch, "E101.0.5.2", {"start": v(244.93, 43.96) * mm, "end": v(244.93, 37.46) * mm});
            skLineSegment(sketch, "E101.0.5.3", {"start": v(244.93, 37.46) * mm, "end": v(251.43, 37.46) * mm});
            skLineSegment(sketch, "E101.0.5.4", {"start": v(244.93, 43.96) * mm, "end": v(251.43, 43.96) * mm});
            skPoint(sketch, "E101.0.5.5", {"position": v(248.18, 40.7) * mm});
            skLineSegment(sketch, "E101.0.6.0", {"start": v(251.43, 52.25) * mm, "end": v(251.43, 45.75) * mm});
            skPoint(sketch, "E101.0.6.1", {"position": v(248.18, 49) * mm});
            skLineSegment(sketch, "E101.0.6.2", {"start": v(244.93, 52.25) * mm, "end": v(244.93, 45.75) * mm});
            skLineSegment(sketch, "E101.0.6.3", {"start": v(244.93, 45.75) * mm, "end": v(251.43, 45.75) * mm});
            skLineSegment(sketch, "E101.0.6.4", {"start": v(244.93, 52.25) * mm, "end": v(251.43, 52.25) * mm});
            skPoint(sketch, "E101.0.6.5", {"position": v(248.18, 49) * mm});
            skLineSegment(sketch, "E101.0.7.0", {"start": v(251.43, 60.53) * mm, "end": v(251.43, 54.03) * mm});
            skPoint(sketch, "E101.0.7.1", {"position": v(248.18, 57.28) * mm});
            skLineSegment(sketch, "E101.0.7.2", {"start": v(244.93, 60.53) * mm, "end": v(244.93, 54.03) * mm});
            skLineSegment(sketch, "E101.0.7.3", {"start": v(244.93, 54.03) * mm, "end": v(251.43, 54.03) * mm});
            skLineSegment(sketch, "E101.0.7.4", {"start": v(244.93, 60.53) * mm, "end": v(251.43, 60.53) * mm});
            skPoint(sketch, "E101.0.7.5", {"position": v(248.18, 57.28) * mm});
            skLineSegment(sketch, "E101.direction1", {"start": v(251.43, -3.98) * mm, "end": v(276.83, -3.98) * mm, "construction": true});
            skLineSegment(sketch, "E101.direction2", {"start": v(251.43, -3.98) * mm, "end": v(251.43, 4.3) * mm, "construction": true});
            skLineSegment(sketch, "E102.0.1.0", {"start": v(260.8, 10.6) * mm, "end": v(260.8, 4.1) * mm});
            skLineSegment(sketch, "E102.0.1.1", {"start": v(267.3, 10.6) * mm, "end": v(267.3, 4.1) * mm});
            skLineSegment(sketch, "E102.0.1.2", {"start": v(260.8, 10.6) * mm, "end": v(267.3, 10.6) * mm});
            skLineSegment(sketch, "E102.0.1.3", {"start": v(260.8, 4.1) * mm, "end": v(267.3, 4.1) * mm});
            skLineSegment(sketch, "E102.0.2.0", {"start": v(260.8, 18.94) * mm, "end": v(260.8, 12.44) * mm});
            skLineSegment(sketch, "E102.0.2.1", {"start": v(267.3, 18.94) * mm, "end": v(267.3, 12.44) * mm});
            skLineSegment(sketch, "E102.0.2.2", {"start": v(260.8, 18.94) * mm, "end": v(267.3, 18.94) * mm});
            skLineSegment(sketch, "E102.0.2.3", {"start": v(260.8, 12.44) * mm, "end": v(267.3, 12.44) * mm});
            skPoint(sketch, "E102.0.2.4", {"position": v(264.05, 15.7) * mm});
            skPoint(sketch, "E102.0.2.5", {"position": v(264.05, 15.7) * mm});
            skLineSegment(sketch, "E102.0.3.0", {"start": v(260.8, 27.3) * mm, "end": v(260.8, 20.8) * mm});
            skLineSegment(sketch, "E102.0.3.1", {"start": v(267.3, 27.3) * mm, "end": v(267.3, 20.8) * mm});
            skLineSegment(sketch, "E102.0.3.2", {"start": v(260.8, 27.3) * mm, "end": v(267.3, 27.3) * mm});
            skLineSegment(sketch, "E102.0.3.3", {"start": v(260.8, 20.8) * mm, "end": v(267.3, 20.8) * mm});
            skPoint(sketch, "E102.0.3.4", {"position": v(264.05, 24.04) * mm});
            skPoint(sketch, "E102.0.3.5", {"position": v(264.05, 24.04) * mm});
            skLineSegment(sketch, "E102.0.4.0", {"start": v(260.8, 35.64) * mm, "end": v(260.8, 29.14) * mm});
            skLineSegment(sketch, "E102.0.4.1", {"start": v(267.3, 35.64) * mm, "end": v(267.3, 29.14) * mm});
            skLineSegment(sketch, "E102.0.4.2", {"start": v(260.8, 35.64) * mm, "end": v(267.3, 35.64) * mm});
            skLineSegment(sketch, "E102.0.4.3", {"start": v(260.8, 29.14) * mm, "end": v(267.3, 29.14) * mm});
            skPoint(sketch, "E102.0.4.4", {"position": v(264.05, 32.4) * mm});
            skPoint(sketch, "E102.0.4.5", {"position": v(264.05, 32.4) * mm});
            skLineSegment(sketch, "E102.0.5.0", {"start": v(260.8, 44) * mm, "end": v(260.8, 37.5) * mm});
            skLineSegment(sketch, "E102.0.5.1", {"start": v(267.3, 44) * mm, "end": v(267.3, 37.5) * mm});
            skLineSegment(sketch, "E102.0.5.2", {"start": v(260.8, 44) * mm, "end": v(267.3, 44) * mm});
            skLineSegment(sketch, "E102.0.5.3", {"start": v(260.8, 37.5) * mm, "end": v(267.3, 37.5) * mm});
            skPoint(sketch, "E102.0.5.4", {"position": v(264.05, 40.74) * mm});
            skPoint(sketch, "E102.0.5.5", {"position": v(264.05, 40.74) * mm});
            skLineSegment(sketch, "E102.0.6.0", {"start": v(260.8, 52.34) * mm, "end": v(260.8, 45.84) * mm});
            skLineSegment(sketch, "E102.0.6.1", {"start": v(267.3, 52.34) * mm, "end": v(267.3, 45.84) * mm});
            skLineSegment(sketch, "E102.0.6.2", {"start": v(260.8, 52.34) * mm, "end": v(267.3, 52.34) * mm});
            skLineSegment(sketch, "E102.0.6.3", {"start": v(260.8, 45.84) * mm, "end": v(267.3, 45.84) * mm});
            skPoint(sketch, "E102.0.6.4", {"position": v(264.05, 49.09) * mm});
            skPoint(sketch, "E102.0.6.5", {"position": v(264.05, 49.09) * mm});
            skLineSegment(sketch, "E102.0.7.0", {"start": v(260.8, 60.69) * mm, "end": v(260.8, 54.19) * mm});
            skLineSegment(sketch, "E102.0.7.1", {"start": v(267.3, 60.69) * mm, "end": v(267.3, 54.19) * mm});
            skLineSegment(sketch, "E102.0.7.2", {"start": v(260.8, 60.69) * mm, "end": v(267.3, 60.69) * mm});
            skLineSegment(sketch, "E102.0.7.3", {"start": v(260.8, 54.19) * mm, "end": v(267.3, 54.19) * mm});
            skPoint(sketch, "E102.0.7.4", {"position": v(264.05, 57.44) * mm});
            skPoint(sketch, "E102.0.7.5", {"position": v(264.05, 57.44) * mm});
            skLineSegment(sketch, "E102.direction1", {"start": v(260.8, -4.25) * mm, "end": v(286.2, -4.25) * mm, "construction": true});
            skLineSegment(sketch, "E102.direction2", {"start": v(260.8, -4.25) * mm, "end": v(260.8, 4.1) * mm, "construction": true});
            skLineSegment(sketch, "E103.0.1.0", {"start": v(279.2, 3.89) * mm, "end": v(285.7, 3.89) * mm});
            skLineSegment(sketch, "E103.0.1.1", {"start": v(279.2, 10.39) * mm, "end": v(279.2, 3.89) * mm});
            skLineSegment(sketch, "E103.0.1.2", {"start": v(279.2, 10.39) * mm, "end": v(285.7, 10.39) * mm});
            skLineSegment(sketch, "E103.0.1.3", {"start": v(285.7, 10.39) * mm, "end": v(285.7, 3.89) * mm});
            skPoint(sketch, "E103.0.1.4", {"position": v(282.45, 7.14) * mm});
            skPoint(sketch, "E103.0.1.5", {"position": v(282.45, 7.14) * mm});
            skLineSegment(sketch, "E103.0.2.0", {"start": v(279.2, 12.34) * mm, "end": v(285.7, 12.34) * mm});
            skLineSegment(sketch, "E103.0.2.1", {"start": v(279.2, 18.84) * mm, "end": v(279.2, 12.34) * mm});
            skLineSegment(sketch, "E103.0.2.2", {"start": v(279.2, 18.84) * mm, "end": v(285.7, 18.84) * mm});
            skLineSegment(sketch, "E103.0.2.3", {"start": v(285.7, 18.84) * mm, "end": v(285.7, 12.34) * mm});
            skPoint(sketch, "E103.0.2.4", {"position": v(282.45, 15.6) * mm});
            skPoint(sketch, "E103.0.2.5", {"position": v(282.45, 15.6) * mm});
            skLineSegment(sketch, "E103.0.3.0", {"start": v(279.2, 20.8) * mm, "end": v(285.7, 20.8) * mm});
            skLineSegment(sketch, "E103.0.3.1", {"start": v(279.2, 27.3) * mm, "end": v(279.2, 20.8) * mm});
            skLineSegment(sketch, "E103.0.3.2", {"start": v(279.2, 27.3) * mm, "end": v(285.7, 27.3) * mm});
            skLineSegment(sketch, "E103.0.3.3", {"start": v(285.7, 27.3) * mm, "end": v(285.7, 20.8) * mm});
            skPoint(sketch, "E103.0.3.4", {"position": v(282.45, 24.05) * mm});
            skPoint(sketch, "E103.0.3.5", {"position": v(282.45, 24.05) * mm});
            skLineSegment(sketch, "E103.0.4.0", {"start": v(279.2, 29.25) * mm, "end": v(285.7, 29.25) * mm});
            skLineSegment(sketch, "E103.0.4.1", {"start": v(279.2, 35.75) * mm, "end": v(279.2, 29.25) * mm});
            skLineSegment(sketch, "E103.0.4.2", {"start": v(279.2, 35.75) * mm, "end": v(285.7, 35.75) * mm});
            skLineSegment(sketch, "E103.0.4.3", {"start": v(285.7, 35.75) * mm, "end": v(285.7, 29.25) * mm});
            skPoint(sketch, "E103.0.4.4", {"position": v(282.45, 32.5) * mm});
            skPoint(sketch, "E103.0.4.5", {"position": v(282.45, 32.5) * mm});
            skLineSegment(sketch, "E103.0.5.0", {"start": v(279.2, 37.7) * mm, "end": v(285.7, 37.7) * mm});
            skLineSegment(sketch, "E103.0.5.1", {"start": v(279.2, 44.2) * mm, "end": v(279.2, 37.7) * mm});
            skLineSegment(sketch, "E103.0.5.2", {"start": v(279.2, 44.2) * mm, "end": v(285.7, 44.2) * mm});
            skLineSegment(sketch, "E103.0.5.3", {"start": v(285.7, 44.2) * mm, "end": v(285.7, 37.7) * mm});
            skPoint(sketch, "E103.0.5.4", {"position": v(282.45, 40.96) * mm});
            skPoint(sketch, "E103.0.5.5", {"position": v(282.45, 40.96) * mm});
            skLineSegment(sketch, "E103.0.6.0", {"start": v(279.2, 46.16) * mm, "end": v(285.7, 46.16) * mm});
            skLineSegment(sketch, "E103.0.6.1", {"start": v(279.2, 52.66) * mm, "end": v(279.2, 46.16) * mm});
            skLineSegment(sketch, "E103.0.6.2", {"start": v(279.2, 52.66) * mm, "end": v(285.7, 52.66) * mm});
            skLineSegment(sketch, "E103.0.6.3", {"start": v(285.7, 52.66) * mm, "end": v(285.7, 46.16) * mm});
            skPoint(sketch, "E103.0.6.4", {"position": v(282.45, 49.41) * mm});
            skPoint(sketch, "E103.0.6.5", {"position": v(282.45, 49.41) * mm});
            skLineSegment(sketch, "E103.0.7.0", {"start": v(279.2, 54.62) * mm, "end": v(285.7, 54.62) * mm});
            skLineSegment(sketch, "E103.0.7.1", {"start": v(279.2, 61.12) * mm, "end": v(279.2, 54.62) * mm});
            skLineSegment(sketch, "E103.0.7.2", {"start": v(279.2, 61.12) * mm, "end": v(285.7, 61.12) * mm});
            skLineSegment(sketch, "E103.0.7.3", {"start": v(285.7, 61.12) * mm, "end": v(285.7, 54.62) * mm});
            skPoint(sketch, "E103.0.7.4", {"position": v(282.45, 57.87) * mm});
            skPoint(sketch, "E103.0.7.5", {"position": v(282.45, 57.87) * mm});
            skLineSegment(sketch, "E103.direction1", {"start": v(279.2, -4.57) * mm, "end": v(304.6, -4.57) * mm, "construction": true});
            skLineSegment(sketch, "E103.direction2", {"start": v(279.2, -4.57) * mm, "end": v(279.2, 3.89) * mm, "construction": true});
            skPoint(sketch, "E104.0.1.0", {"position": v(298.33, 6.93) * mm});
            skLineSegment(sketch, "E104.0.1.1", {"start": v(295.08, 3.68) * mm, "end": v(301.58, 3.68) * mm});
            skLineSegment(sketch, "E104.0.1.2", {"start": v(295.08, 10.18) * mm, "end": v(301.58, 10.18) * mm});
            skPoint(sketch, "E104.0.1.3", {"position": v(304.8, 2.55) * mm});
            skLineSegment(sketch, "E104.0.1.4", {"start": v(295.08, 10.18) * mm, "end": v(295.08, 3.68) * mm});
            skLineSegment(sketch, "E104.0.1.5", {"start": v(301.58, 10.18) * mm, "end": v(301.58, 3.68) * mm});
            skPoint(sketch, "E104.0.1.6", {"position": v(298.33, 6.93) * mm});
            skPoint(sketch, "E104.0.2.0", {"position": v(298.33, 15.45) * mm});
            skLineSegment(sketch, "E104.0.2.1", {"start": v(295.08, 12.2) * mm, "end": v(301.58, 12.2) * mm});
            skLineSegment(sketch, "E104.0.2.2", {"start": v(295.08, 18.7) * mm, "end": v(301.58, 18.7) * mm});
            skPoint(sketch, "E104.0.2.3", {"position": v(304.8, 11.06) * mm});
            skLineSegment(sketch, "E104.0.2.4", {"start": v(295.08, 18.7) * mm, "end": v(295.08, 12.2) * mm});
            skLineSegment(sketch, "E104.0.2.5", {"start": v(301.58, 18.7) * mm, "end": v(301.58, 12.2) * mm});
            skPoint(sketch, "E104.0.2.6", {"position": v(298.33, 15.45) * mm});
            skPoint(sketch, "E104.0.3.0", {"position": v(298.33, 23.97) * mm});
            skLineSegment(sketch, "E104.0.3.1", {"start": v(295.08, 20.72) * mm, "end": v(301.58, 20.72) * mm});
            skLineSegment(sketch, "E104.0.3.2", {"start": v(295.08, 27.22) * mm, "end": v(301.58, 27.22) * mm});
            skPoint(sketch, "E104.0.3.3", {"position": v(304.8, 19.58) * mm});
            skLineSegment(sketch, "E104.0.3.4", {"start": v(295.08, 27.22) * mm, "end": v(295.08, 20.72) * mm});
            skLineSegment(sketch, "E104.0.3.5", {"start": v(301.58, 27.22) * mm, "end": v(301.58, 20.72) * mm});
            skPoint(sketch, "E104.0.3.6", {"position": v(298.33, 23.97) * mm});
            skPoint(sketch, "E104.0.4.0", {"position": v(298.33, 32.48) * mm});
            skLineSegment(sketch, "E104.0.4.1", {"start": v(295.08, 29.23) * mm, "end": v(301.58, 29.23) * mm});
            skLineSegment(sketch, "E104.0.4.2", {"start": v(295.08, 35.73) * mm, "end": v(301.58, 35.73) * mm});
            skPoint(sketch, "E104.0.4.3", {"position": v(304.8, 28.1) * mm});
            skLineSegment(sketch, "E104.0.4.4", {"start": v(295.08, 35.73) * mm, "end": v(295.08, 29.23) * mm});
            skLineSegment(sketch, "E104.0.4.5", {"start": v(301.58, 35.73) * mm, "end": v(301.58, 29.23) * mm});
            skPoint(sketch, "E104.0.4.6", {"position": v(298.33, 32.48) * mm});
            skPoint(sketch, "E104.0.5.0", {"position": v(298.33, 41) * mm});
            skLineSegment(sketch, "E104.0.5.1", {"start": v(295.08, 37.75) * mm, "end": v(301.58, 37.75) * mm});
            skLineSegment(sketch, "E104.0.5.2", {"start": v(295.08, 44.25) * mm, "end": v(301.58, 44.25) * mm});
            skPoint(sketch, "E104.0.5.3", {"position": v(304.8, 36.62) * mm});
            skLineSegment(sketch, "E104.0.5.4", {"start": v(295.08, 44.25) * mm, "end": v(295.08, 37.75) * mm});
            skLineSegment(sketch, "E104.0.5.5", {"start": v(301.58, 44.25) * mm, "end": v(301.58, 37.75) * mm});
            skPoint(sketch, "E104.0.5.6", {"position": v(298.33, 41) * mm});
            skPoint(sketch, "E104.0.6.0", {"position": v(298.33, 49.52) * mm});
            skLineSegment(sketch, "E104.0.6.1", {"start": v(295.08, 46.27) * mm, "end": v(301.58, 46.27) * mm});
            skLineSegment(sketch, "E104.0.6.2", {"start": v(295.08, 52.77) * mm, "end": v(301.58, 52.77) * mm});
            skPoint(sketch, "E104.0.6.3", {"position": v(304.8, 45.14) * mm});
            skLineSegment(sketch, "E104.0.6.4", {"start": v(295.08, 52.77) * mm, "end": v(295.08, 46.27) * mm});
            skLineSegment(sketch, "E104.0.6.5", {"start": v(301.58, 52.77) * mm, "end": v(301.58, 46.27) * mm});
            skPoint(sketch, "E104.0.6.6", {"position": v(298.33, 49.52) * mm});
            skPoint(sketch, "E104.0.7.0", {"position": v(298.33, 58.04) * mm});
            skLineSegment(sketch, "E104.0.7.1", {"start": v(295.08, 54.8) * mm, "end": v(301.58, 54.8) * mm});
            skLineSegment(sketch, "E104.0.7.2", {"start": v(295.08, 61.3) * mm, "end": v(301.58, 61.3) * mm});
            skPoint(sketch, "E104.0.7.3", {"position": v(304.8, 53.66) * mm});
            skLineSegment(sketch, "E104.0.7.4", {"start": v(295.08, 61.3) * mm, "end": v(295.08, 54.8) * mm});
            skLineSegment(sketch, "E104.0.7.5", {"start": v(301.58, 61.3) * mm, "end": v(301.58, 54.8) * mm});
            skPoint(sketch, "E104.0.7.6", {"position": v(298.33, 58.04) * mm});
            skLineSegment(sketch, "E104.direction1", {"start": v(298.33, -1.6) * mm, "end": v(323.73, -1.6) * mm, "construction": true});
            skLineSegment(sketch, "E104.direction2", {"start": v(298.33, -1.6) * mm, "end": v(298.33, 6.93) * mm, "construction": true});
            skPoint(sketch, "E105", {"position": v(11.11, 10.44) * mm});
            skPoint(sketch, "E106.0.1.0", {"position": v(11.11, 10.43) * mm});
            skPoint(sketch, "E106.0.1.1", {"position": v(11.11, 17.53) * mm});
            skLineSegment(sketch, "E106.0.1.2", {"start": v(7.86, 13.68) * mm, "end": v(7.86, 7.18) * mm});
            skLineSegment(sketch, "E106.0.1.3", {"start": v(7.86, 13.68) * mm, "end": v(14.36, 13.68) * mm});
            skLineSegment(sketch, "E106.0.1.4", {"start": v(7.86, 7.18) * mm, "end": v(14.36, 7.18) * mm});
            skLineSegment(sketch, "E106.0.1.5", {"start": v(14.36, 13.68) * mm, "end": v(14.36, 7.18) * mm});
            skPoint(sketch, "E106.0.1.6", {"position": v(11.11, 10.43) * mm});
            skPoint(sketch, "E106.0.1.7", {"position": v(11.11, 10.43) * mm});
            skPoint(sketch, "E106.0.2.0", {"position": v(11.11, 17.53) * mm});
            skPoint(sketch, "E106.0.2.1", {"position": v(11.11, 24.63) * mm});
            skLineSegment(sketch, "E106.0.2.2", {"start": v(7.86, 20.78) * mm, "end": v(7.86, 14.28) * mm});
            skLineSegment(sketch, "E106.0.2.3", {"start": v(7.86, 20.78) * mm, "end": v(14.36, 20.78) * mm});
            skLineSegment(sketch, "E106.0.2.4", {"start": v(7.86, 14.28) * mm, "end": v(14.36, 14.28) * mm});
            skLineSegment(sketch, "E106.0.2.5", {"start": v(14.36, 20.78) * mm, "end": v(14.36, 14.28) * mm});
            skPoint(sketch, "E106.0.2.6", {"position": v(11.11, 17.53) * mm});
            skPoint(sketch, "E106.0.2.7", {"position": v(11.11, 17.53) * mm});
            skPoint(sketch, "E106.0.3.0", {"position": v(11.11, 24.62) * mm});
            skPoint(sketch, "E106.0.3.1", {"position": v(11.11, 31.73) * mm});
            skLineSegment(sketch, "E106.0.3.2", {"start": v(7.86, 27.87) * mm, "end": v(7.86, 21.37) * mm});
            skLineSegment(sketch, "E106.0.3.3", {"start": v(7.86, 27.87) * mm, "end": v(14.36, 27.87) * mm});
            skLineSegment(sketch, "E106.0.3.4", {"start": v(7.86, 21.37) * mm, "end": v(14.36, 21.37) * mm});
            skLineSegment(sketch, "E106.0.3.5", {"start": v(14.36, 27.87) * mm, "end": v(14.36, 21.37) * mm});
            skPoint(sketch, "E106.0.3.6", {"position": v(11.11, 24.62) * mm});
            skPoint(sketch, "E106.0.3.7", {"position": v(11.11, 24.62) * mm});
            skPoint(sketch, "E106.0.4.0", {"position": v(11.11, 31.72) * mm});
            skPoint(sketch, "E106.0.4.1", {"position": v(11.11, 38.82) * mm});
            skLineSegment(sketch, "E106.0.4.2", {"start": v(7.86, 34.97) * mm, "end": v(7.86, 28.47) * mm});
            skLineSegment(sketch, "E106.0.4.3", {"start": v(7.86, 34.97) * mm, "end": v(14.36, 34.97) * mm});
            skLineSegment(sketch, "E106.0.4.4", {"start": v(7.86, 28.47) * mm, "end": v(14.36, 28.47) * mm});
            skLineSegment(sketch, "E106.0.4.5", {"start": v(14.36, 34.97) * mm, "end": v(14.36, 28.47) * mm});
            skPoint(sketch, "E106.0.4.6", {"position": v(11.11, 31.72) * mm});
            skPoint(sketch, "E106.0.4.7", {"position": v(11.11, 31.72) * mm});
            skPoint(sketch, "E106.0.5.0", {"position": v(11.11, 38.82) * mm});
            skPoint(sketch, "E106.0.5.1", {"position": v(11.11, 45.92) * mm});
            skLineSegment(sketch, "E106.0.5.2", {"start": v(7.86, 42.07) * mm, "end": v(7.86, 35.57) * mm});
            skLineSegment(sketch, "E106.0.5.3", {"start": v(7.86, 42.07) * mm, "end": v(14.36, 42.07) * mm});
            skLineSegment(sketch, "E106.0.5.4", {"start": v(7.86, 35.57) * mm, "end": v(14.36, 35.57) * mm});
            skLineSegment(sketch, "E106.0.5.5", {"start": v(14.36, 42.07) * mm, "end": v(14.36, 35.57) * mm});
            skPoint(sketch, "E106.0.5.6", {"position": v(11.11, 38.82) * mm});
            skPoint(sketch, "E106.0.5.7", {"position": v(11.11, 38.82) * mm});
            skPoint(sketch, "E106.0.6.0", {"position": v(11.11, 45.92) * mm});
            skPoint(sketch, "E106.0.6.1", {"position": v(11.11, 53.02) * mm});
            skLineSegment(sketch, "E106.0.6.2", {"start": v(7.86, 49.17) * mm, "end": v(7.86, 42.67) * mm});
            skLineSegment(sketch, "E106.0.6.3", {"start": v(7.86, 49.17) * mm, "end": v(14.36, 49.17) * mm});
            skLineSegment(sketch, "E106.0.6.4", {"start": v(7.86, 42.67) * mm, "end": v(14.36, 42.67) * mm});
            skLineSegment(sketch, "E106.0.6.5", {"start": v(14.36, 49.17) * mm, "end": v(14.36, 42.67) * mm});
            skPoint(sketch, "E106.0.6.6", {"position": v(11.11, 45.92) * mm});
            skPoint(sketch, "E106.0.6.7", {"position": v(11.11, 45.92) * mm});
            skPoint(sketch, "E106.0.7.0", {"position": v(11.11, 53.01) * mm});
            skPoint(sketch, "E106.0.7.1", {"position": v(11.11, 60.12) * mm});
            skLineSegment(sketch, "E106.0.7.2", {"start": v(7.86, 56.26) * mm, "end": v(7.86, 49.76) * mm});
            skLineSegment(sketch, "E106.0.7.3", {"start": v(7.86, 56.26) * mm, "end": v(14.36, 56.26) * mm});
            skLineSegment(sketch, "E106.0.7.4", {"start": v(7.86, 49.76) * mm, "end": v(14.36, 49.76) * mm});
            skLineSegment(sketch, "E106.0.7.5", {"start": v(14.36, 56.26) * mm, "end": v(14.36, 49.76) * mm});
            skPoint(sketch, "E106.0.7.6", {"position": v(11.11, 53.01) * mm});
            skPoint(sketch, "E106.0.7.7", {"position": v(11.11, 53.01) * mm});
            skLineSegment(sketch, "E106.direction1", {"start": v(11.11, 3.33) * mm, "end": v(36.11, 3.33) * mm, "construction": true});
            skLineSegment(sketch, "E106.direction2", {"start": v(11.11, 3.33) * mm, "end": v(11.11, 10.43) * mm, "construction": true});
            skLineSegment(sketch, "E107", {"start": v(345.34, -11.78) * mm, "end": v(345.34, 72.6) * mm, "construction": true});
            skLineSegment(sketch, "E108", {"start": v(374.16, -13.41) * mm, "end": v(374.16, 70.78) * mm, "construction": true});
            skLineSegment(sketch, "E109", {"start": v(401.36, -15.95) * mm, "end": v(401.36, 71.14) * mm, "construction": true});
            skLineSegment(sketch, "E110", {"start": v(427.04, -15.77) * mm, "end": v(427.04, 70.78) * mm, "construction": true});
            skLineSegment(sketch, "E111", {"start": v(474.15, -18.13) * mm, "end": v(474.15, 73.32) * mm, "construction": true});
            skLineSegment(sketch, "E112", {"start": v(314.8, -23.18) * mm, "end": v(314.8, 74.56) * mm, "construction": true});
            skPoint(sketch, "E113", {"position": v(314.8, 6.72) * mm});
            skPoint(sketch, "E114", {"position": v(330.68, 6.52) * mm});
            skPoint(sketch, "E115", {"position": v(345.34, 6.34) * mm});
            skPoint(sketch, "E116", {"position": v(361.21, 6.15) * mm});
            skPoint(sketch, "E117", {"position": v(374.16, 5.99) * mm});
            skPoint(sketch, "E118", {"position": v(390.03, 5.8) * mm});
            skPoint(sketch, "E119", {"position": v(390.06, 5.7) * mm});
            skPoint(sketch, "E120", {"position": v(401.36, 5.66) * mm});
            skPoint(sketch, "E121", {"position": v(417.24, 5.46) * mm});
            skPoint(sketch, "E122", {"position": v(417.22, 5.44) * mm});
            skLineSegment(sketch, "E123", {"start": v(617.23, -23.82) * mm, "end": v(617.23, 80.23) * mm, "construction": true});
            skSolve(sketch);
        }
        {
            var Q0;
            Q0=qSketchRegion(id+"F0",true);
            extrude(context, id + "F1", {"entities" : qUnion([Q0]), "depth" : 1.52 * mm});
        }
        {
            var Q0;
            Q0=makeQuery(id+"F1.opExtrude","CAP_FACE",FACE,{"disambiguationData":[OSD([sQuery(id+"F0.wireOp",EDGE,"E0"),sQuery(id+"F0.wireOp",EDGE,"E1"),sQuery(id+"F0.wireOp",EDGE,"E2"),sQuery(id+"F0.wireOp",EDGE,"E3")])],"isStart":false});
            var sketch = newSketch(context, id + "F2", { "sketchPlane" : qUnion([Q0])});
            skLineSegment(sketch, "E124", {"start": v(0, 28.2) * mm, "end": v(635, 28.2) * mm, "construction": true});
            skSolve(sketch);
        }
        {
            var Q0;
            Q0=makeQuery(id+"F2.imprint","IMPRINT",FACE,{"disambiguationData":[TD([[makeQuery(id+"F2.imprint","IMPRINT",EDGE,{"derivedFrom":makeQuery(id+"F1.opExtrude","CAP_EDGE",EDGE,{"disambiguationData":[OSD([sQuery(id+"F0.wireOp",EDGE,"E0")])],"isStart":false})}),-1.0]])]});
            var sketch = newSketch(context, id + "F3", { "sketchPlane" : qUnion([Q0])});
            skCircle(sketch, "E125", {"center": v(97.4, 8.08) * mm, "radius": 1.13 * mm});
            skLineSegment(sketch, "E126", {"start": v(0, 8.12) * mm, "end": v(635, 7.87) * mm, "construction": true});
            skCircle(sketch, "E127", {"center": v(3.18, 8.12) * mm, "radius": 1.13 * mm});
            skCircle(sketch, "E128", {"center": v(181.33, 8.05) * mm, "radius": 1.13 * mm});
            skCircle(sketch, "E129", {"center": v(290.4, 8) * mm, "radius": 1.13 * mm});
            skCircle(sketch, "E130", {"center": v(409.3, 7.96) * mm, "radius": 1.13 * mm});
            skCircle(sketch, "E131", {"center": v(524.06, 7.92) * mm, "radius": 1.13 * mm});
            skCircle(sketch, "E132", {"center": v(624.44, 7.88) * mm, "radius": 1.13 * mm});
            skCircle(sketch, "E133.MirrorC", {"center": v(97.4, 48.3) * mm, "radius": 1.13 * mm});
            skCircle(sketch, "E134.MirrorC", {"center": v(3.18, 48.27) * mm, "radius": 1.13 * mm});
            skCircle(sketch, "E135.MirrorC", {"center": v(181.33, 48.34) * mm, "radius": 1.13 * mm});
            skCircle(sketch, "E136.MirrorC", {"center": v(290.4, 48.38) * mm, "radius": 1.13 * mm});
            skCircle(sketch, "E137.MirrorC", {"center": v(409.3, 48.43) * mm, "radius": 1.13 * mm});
            skCircle(sketch, "E138.MirrorC", {"center": v(524.06, 48.47) * mm, "radius": 1.13 * mm});
            skCircle(sketch, "E139.MirrorC", {"center": v(624.44, 48.5) * mm, "radius": 1.13 * mm});
            skSolve(sketch);
        }
        {
            var Q0;
            Q0=qSketchRegion(id+"F3",true);
            extrude(context, id + "F4", {"entities" : qUnion([Q0]), "operationType" : NewBodyOperationType.REMOVE, "endBound" : BoundingType.THROUGH_ALL, "depth" : 25.4 * mm});
        }
    });
